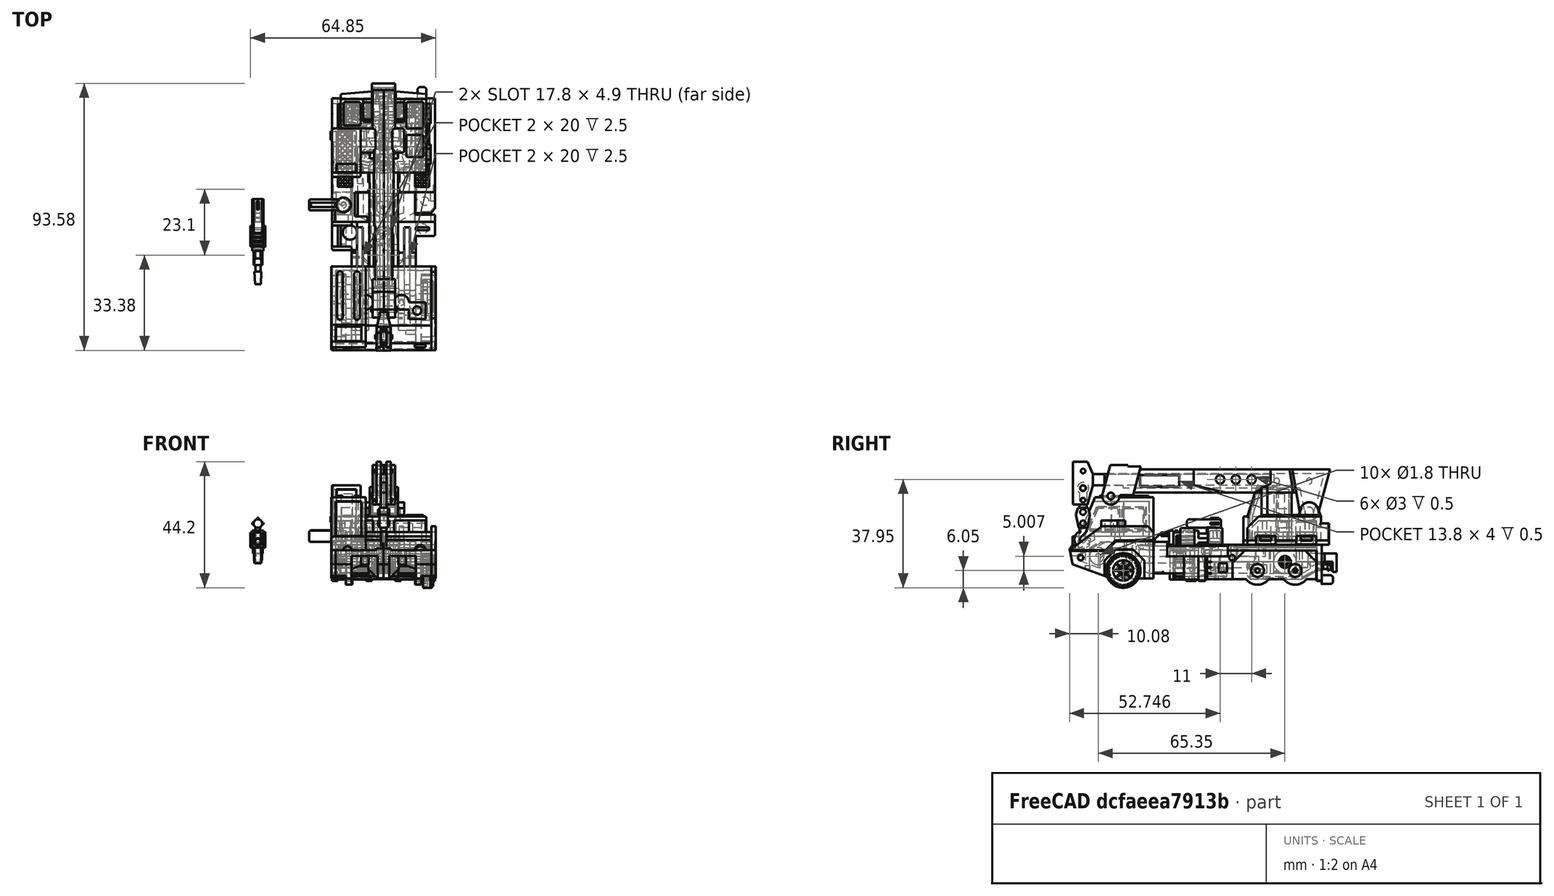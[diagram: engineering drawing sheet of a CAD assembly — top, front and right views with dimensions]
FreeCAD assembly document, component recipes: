
FREECAD ASSEMBLY — COMPONENT RECIPES ("Hook")

This assembly document has 27 components, labeled P0..P26 below (a component is one placed body or linked part). 27 of them carry a construction recipe — the FreeCAD feature program that regenerates the part from scratch, quoted from this document or its linked companion documents; the rest are supplied as boundary geometry only. No exploded tour is included for this assembly.
NOTE — document 2 of 5 of this assembly tour. The two overview renders and the header above are repeated from document 1; the component sections below continue where the previous document stopped.
COMPONENT P7 — recipe-attached ("Swivel_Base", modeled in this document).
Construction recipe (the document's own serialized feature program — sketch geometry with constraints, then the solid features built on it; lengths are millimeters unless a unit is written):

FEATURE [PartDesign::SubShapeBinder] Binder002
  BindCopyOnChange = 0
  BindMode = 2
  ClaimChildren = false
  Context = -> Body007 [Binder002.]
  Fuse = false
  MakeFace = true
  OffsetFill = false
  OffsetIntersection = false
  OffsetJoinType = 0
  OffsetOpenResult = false
  PartialLoad = false
  Refine = true
  Relative = true
  _Version = 2
FEATURE [Sketcher::SketchObject] Sketch080
  ArcFitTolerance = 1e-06
  AttachmentSupport = -> [Binder002]
  ExternalGeometry = -> [Binder002]
  FullyConstrained = true
  MakeInternals = false
  MapMode = 5
  Placement = pos=(0,0,5) rot=(0,0,1;0rad)
  sketch-geometry (2):
    g0: Circle CenterX=18.1 CenterY=30.5 CenterZ=0 NormalX=0 NormalY=0 NormalZ=1 AngleXU=0 Radius=5.55
    g1: Circle CenterX=18.1 CenterY=30.5 CenterZ=0 NormalX=0 NormalY=0 NormalZ=1 AngleXU=0 Radius=7
  constraints (6):
    c: Coincident(g0,g-4)
    c: Diameter(g-3) = 11
    c: Diameter(g-4) = 5
    c: Diameter(g0) = 11.1
    c: Coincident(g1,g0)
    c: Diameter(g1) = 14
FEATURE [PartDesign::Pad] Pad058
  Direction = (0,0,1)
  Length = 3
  Length2 = 10
  Profile = -> Sketch080
  ReferenceAxis = -> Sketch080 [N_Axis]
  Refine = true
  Reversed = true
  Suppressed = false
  Type = 0
FEATURE [Sketcher::SketchObject] Sketch081
  ArcFitTolerance = 1e-06
  AttachmentSupport = -> [Pad058]
  ExternalGeometry = -> [Pad058]
  FullyConstrained = true
  MakeInternals = false
  MapMode = 5
  Placement = pos=(0,0,5) rot=(0,0,1;0rad)
  sketch-geometry (1):
    g0: Circle CenterX=18.1 CenterY=30.5 CenterZ=0 NormalX=0 NormalY=0 NormalZ=1 AngleXU=0 Radius=7
  constraints (2):
    c: Coincident(g0,g-3)
    c: Equal(g0,g-3)
FEATURE [PartDesign::Pad] Pad059
  BaseFeature = -> Pad058
  Direction = (0,0,1)
  Length = 1.5
  Length2 = 10
  Profile = -> Sketch081
  ReferenceAxis = -> Sketch081 [N_Axis]
  Refine = true
  Suppressed = false
  Type = 0
FEATURE [Sketcher::SketchObject] Sketch082
  ArcFitTolerance = 1e-06
  AttachmentSupport = -> [Pad059]
  ExternalGeometry = -> [Pad059]
  FullyConstrained = true
  MakeInternals = false
  MapMode = 5
  Placement = pos=(0,0,6.5) rot=(0,0,1;0rad)
  sketch-geometry (1):
    g0: Circle CenterX=18.1 CenterY=30.5 CenterZ=0 NormalX=0 NormalY=0 NormalZ=1 AngleXU=0 Radius=2.25
  constraints (2):
    c: Coincident(g0,g-3)
    c: Diameter(g0) = 4.5
FEATURE [PartDesign::Pad] Pad060
  BaseFeature = -> Pad059
  Direction = (0,0,1)
  Length = 1.5
  Length2 = 10
  Profile = -> Sketch082
  ReferenceAxis = -> Sketch082 [N_Axis]
  Refine = true
  Suppressed = false
  Type = 0
FEATURE [Sketcher::SketchObject] Sketch083
  ArcFitTolerance = 1e-06
  AttachmentSupport = -> [Pad060]
  ExternalGeometry = -> [Pad060]
  FullyConstrained = true
  MakeInternals = false
  MapMode = 5
  Placement = pos=(0,0,8) rot=(0,0,1;0rad)
  sketch-geometry (1):
    g0: Circle CenterX=18.1 CenterY=30.5 CenterZ=0 NormalX=0 NormalY=0 NormalZ=1 AngleXU=0 Radius=0.75
  constraints (2):
    c: Coincident(g0,g-3)
    c: Diameter(g0) = 1.5
FEATURE [PartDesign::Pocket] Pocket032
  BaseFeature = -> Pad060
  Direction = (0,0,-1)
  Length = 5
  Length2 = 5
  Profile = -> Sketch083
  ReferenceAxis = -> Sketch083 [N_Axis]
  Refine = true
  Suppressed = false
  Type = 0
FEATURE [Sketcher::SketchObject] Sketch084
  ArcFitTolerance = 1e-06
  AttachmentSupport = -> [Pocket032]
  ExternalGeometry = -> [Pocket032]
  FullyConstrained = true
  MakeInternals = false
  MapMode = 5
  Placement = pos=(0,0,5) rot=(1,0,0;3.14159rad)
  sketch-geometry (1):
    g0: Circle CenterX=18.1 CenterY=-30.5 CenterZ=0 NormalX=0 NormalY=0 NormalZ=1 AngleXU=0 Radius=2.35
  constraints (2):
    c: Coincident(g0,g-4)
    c: Diameter(g0) = 4.7
FEATURE [PartDesign::Pad] Pad061
  BaseFeature = -> Pocket032
  Direction = (0,0,-1)
  Length = 3
  Length2 = 10
  Profile = -> Sketch084
  ReferenceAxis = -> Sketch084 [N_Axis]
  Refine = true
  Suppressed = false
  Type = 0
FEATURE [Sketcher::SketchObject] Sketch085
  ArcFitTolerance = 1e-06
  AttachmentSupport = -> [Pad061]
  ExternalGeometry = -> [Pad061]
  FullyConstrained = true
  MakeInternals = false
  MapMode = 5
  Placement = pos=(0,0,2) rot=(1,0,0;3.14159rad)
  sketch-geometry (1):
    g0: Circle CenterX=18.1 CenterY=-30.5 CenterZ=0 NormalX=0 NormalY=0 NormalZ=1 AngleXU=0 Radius=0.75
  constraints (2):
    c: Coincident(g0,g-3)
    c: Diameter(g0) = 1.5
FEATURE [PartDesign::Pocket] Pocket033
  BaseFeature = -> Pad061
  Direction = (0,0,1)
  Length = 5
  Length2 = 5
  Profile = -> Sketch085
  ReferenceAxis = -> Sketch085 [N_Axis]
  Refine = true
  Suppressed = false
  Type = 0
FEATURE [Sketcher::SketchObject] Sketch086
  ArcFitTolerance = 1e-06
  AttachmentSupport = -> [Pocket033]
  ExternalGeometry = -> [Pocket033]
  FullyConstrained = true
  MakeInternals = false
  MapMode = 5
  Placement = pos=(0,0,2) rot=(1,0,0;3.14159rad)
  sketch-geometry (9):
    g0: LineSegment StartX=33 StartY=-17.25 StartZ=0 EndX=10 EndY=-17.25 EndZ=0
    g1: LineSegment StartX=10 StartY=-17.25 StartZ=0 EndX=10 EndY=-15.75 EndZ=0
    g2: LineSegment StartX=10 StartY=-15.75 StartZ=0 EndX=0 EndY=-15.75 EndZ=0
    g3: LineSegment StartX=0 StartY=-15.75 StartZ=0 EndX=0 EndY=-32.75 EndZ=0
    g4: LineSegment StartX=0 StartY=-32.75 StartZ=0 EndX=3 EndY=-32.75 EndZ=0
    g5: LineSegment StartX=3 StartY=-32.75 StartZ=0 EndX=3 EndY=-45.75 EndZ=0
    g6: LineSegment StartX=3 StartY=-45.75 StartZ=0 EndX=33 EndY=-45.75 EndZ=0
    g7: LineSegment StartX=33 StartY=-45.75 StartZ=0 EndX=33 EndY=-17.25 EndZ=0
    g8: LineSegment [constr] StartX=18.1 StartY=-30.5 StartZ=0 EndX=18.1 EndY=-23.5 EndZ=0
  constraints (27):
    c: Horizontal(g0)
    c: Coincident(g1,g0)
    c: Vertical(g1)
    c: PointOnObject(g2,g-2)
    c: Horizontal(g2)
    c: Coincident(g3,g2)
    c: PointOnObject(g3,g-2)
    c: Coincident(g4,g3)
    c: Horizontal(g4)
    c: Coincident(g5,g4)
    c: Vertical(g5)
    c: Coincident(g6,g5)
    c: Horizontal(g6)
    c: Coincident(g7,g6)
    c: Coincident(g7,g0)
    c: Vertical(g7)
    c: DistanceX(g2,g2) = 10
    c: DistanceY(g3,g3) = 17
    c: Coincident(g2,g1)
    c: DistanceY(g1,g1) = 1.5
    c: DistanceY(g5,g5) = 13
    c: DistanceX(g4,g4) = 3
    c: DistanceX(g6,g6) = 30
    c: Coincident(g8,g-3)
    c: PointOnObject(g8,g-3)
    c: Vertical(g8)
    c: DistanceY(g8,g0) = 6.25
FEATURE [PartDesign::Pad] Pad062
  BaseFeature = -> Pocket033
  Direction = (0,0,-1)
  Length = 1.5
  Length2 = 10
  Profile = -> Sketch086
  ReferenceAxis = -> Sketch086 [N_Axis]
  Refine = true
  Reversed = true
  Suppressed = false
  Type = 0
FEATURE [Sketcher::SketchObject] Sketch087
  ArcFitTolerance = 1e-06
  AttachmentSupport = -> [Pad062]
  ExternalGeometry = -> [Pad062]
  FullyConstrained = true
  MakeInternals = false
  MapMode = 5
  Placement = pos=(0,0,3.5) rot=(0,0,1;0rad)
  sketch-geometry (4):
    g0: LineSegment StartX=14.6 StartY=45.75 StartZ=0 EndX=14.6 EndY=42.95 EndZ=0
    g1: LineSegment StartX=14.6 StartY=42.95 StartZ=0 EndX=21.6 EndY=42.95 EndZ=0
    g2: LineSegment StartX=21.6 StartY=42.95 StartZ=0 EndX=21.6 EndY=45.75 EndZ=0
    g3: LineSegment StartX=21.6 StartY=45.75 StartZ=0 EndX=14.6 EndY=45.75 EndZ=0
  constraints (12):
    c: Coincident(g0,g1)
    c: Coincident(g1,g2)
    c: Coincident(g2,g3)
    c: Coincident(g3,g0)
    c: Vertical(g0)
    c: Vertical(g2)
    c: Horizontal(g1)
    c: Horizontal(g3)
    c: PointOnObject(g0,g-3)
    c: DistanceX(g3,g3) = 7
    c: DistanceY(g2,g2) = 2.8
    c: DistanceX(g0,g-4) = 3.5
FEATURE [PartDesign::Pad] Pad063
  BaseFeature = -> Pad062
  Direction = (0,0,1)
  Length = 6
  Length2 = 10
  Profile = -> Sketch087
  ReferenceAxis = -> Sketch087 [N_Axis]
  Refine = true
  Suppressed = false
  Type = 0
FEATURE [Sketcher::SketchObject] Sketch088
  ArcFitTolerance = 1e-06
  AttachmentSupport = -> [Pad063]
  ExternalGeometry = -> [Pad063]
  FullyConstrained = true
  MakeInternals = false
  MapMode = 5
  Placement = pos=(0,0,3.5) rot=(0,0,1;0rad)
  sketch-geometry (2):
    g0: Circle CenterX=18.1 CenterY=38.9 CenterZ=0 NormalX=0 NormalY=0 NormalZ=1 AngleXU=0 Radius=1.55
    g1: Circle CenterX=4.95 CenterY=29.4 CenterZ=0 NormalX=0 NormalY=0 NormalZ=1 AngleXU=0 Radius=1.55
  constraints (6):
    c: Diameter(g0) = 3.1
    c: Diameter(g1) = 3.1
    c: DistanceX(g0,g-4) = 0
    c: DistanceY(g0,g-5) = 4.05
    c: DistanceX(g-6,g1) = 4.95
    c: DistanceY(g-7,g1) = 13.65
FEATURE [PartDesign::Pad] Pad064
  BaseFeature = -> Pad063
  Direction = (0,0,1)
  Length = 6.9
  Length2 = 10
  Profile = -> Sketch088
  ReferenceAxis = -> Sketch088 [N_Axis]
  Refine = true
  Suppressed = false
  Type = 0
FEATURE [Sketcher::SketchObject] Sketch089
  ArcFitTolerance = 1e-06
  AttachmentSupport = -> [Pad064]
  ExternalGeometry = -> [Pad064]
  FullyConstrained = true
  MakeInternals = false
  MapMode = 5
  Placement = pos=(0,0,3.5) rot=(0,0,1;0rad)
  sketch-geometry (8):
    g0: LineSegment StartX=31.5 StartY=39.75 StartZ=0 EndX=31.5 EndY=35.95 EndZ=0
    g1: LineSegment StartX=31.5 StartY=35.95 StartZ=0 EndX=34.5 EndY=35.95 EndZ=0
    g2: LineSegment StartX=34.5 StartY=35.95 StartZ=0 EndX=34.5 EndY=39.75 EndZ=0
    g3: LineSegment StartX=34.5 StartY=39.75 StartZ=0 EndX=31.5 EndY=39.75 EndZ=0
    g4: LineSegment StartX=31.5 StartY=25.55 StartZ=0 EndX=31.5 EndY=21.75 EndZ=0
    g5: LineSegment StartX=31.5 StartY=21.75 StartZ=0 EndX=34.5 EndY=21.75 EndZ=0
    g6: LineSegment StartX=34.5 StartY=21.75 StartZ=0 EndX=34.5 EndY=25.55 EndZ=0
    g7: LineSegment StartX=34.5 StartY=25.55 StartZ=0 EndX=31.5 EndY=25.55 EndZ=0
  constraints (25):
    c: Coincident(g0,g1)
    c: Coincident(g1,g2)
    c: Coincident(g2,g3)
    c: Coincident(g3,g0)
    c: Vertical(g0)
    c: Vertical(g2)
    c: Horizontal(g1)
    c: Horizontal(g3)
    c: Coincident(g4,g5)
    c: Coincident(g5,g6)
    c: Coincident(g6,g7)
    c: Coincident(g7,g4)
    c: Vertical(g4)
    c: Vertical(g6)
    c: Horizontal(g5)
    c: Horizontal(g7)
    c: DistanceY(g6,g6) = 3.8
    c: DistanceY(g2,g2) = 3.8
    c: DistanceX(g3,g3) = 3
    c: DistanceX(g7,g7) = 3
    c: DistanceX(g-5,g6) = 1.5
    c: DistanceX(g-4,g2) = 1.5
    c: DistanceY(g2,g-4) = 6
    c: DistanceY(g4,g0) = 10.4
    c: DistanceY(g-5,g5) = 4.5
FEATURE [PartDesign::Pad] Pad065
  BaseFeature = -> Pad064
  Direction = (0,0,1)
  Length = 1.5
  Length2 = 10
  Profile = -> Sketch089
  ReferenceAxis = -> Sketch089 [N_Axis]
  Refine = true
  Suppressed = false
  Type = 0
FEATURE [PartDesign::Pocket] Pocket034
  BaseFeature = -> Pad065
  Direction = (0,0,-1)
  Length = 8
  Length2 = 5
  Profile = -> Pad065 [Edge86]
  Refine = true
  Suppressed = false
  Type = 0
FEATURE [Sketcher::SketchObject] Sketch090
  ArcFitTolerance = 1e-06
  AttachmentSupport = -> [Pocket034]
  ExternalGeometry = -> [Pocket034]
  FullyConstrained = true
  MakeInternals = false
  MapMode = 5
  Placement = pos=(0,0,2) rot=(1,0,0;3.14159rad)
  sketch-geometry (1):
    g0: Circle CenterX=18.1 CenterY=-30.5 CenterZ=0 NormalX=0 NormalY=0 NormalZ=1 AngleXU=0 Radius=5.55
  constraints (2):
    c: Coincident(g0,g-3)
    c: Diameter(g0) = 11.1
FEATURE [PartDesign::Pocket] Pocket035
  BaseFeature = -> Pocket034
  Direction = (0,0,1)
  Length = 1.5
  Length2 = 5
  Profile = -> Sketch090
  ReferenceAxis = -> Sketch090 [N_Axis]
  Refine = true
  Suppressed = false
  Type = 0
FEATURE [PartDesign::Pad] Pad066
  BaseFeature = -> Pocket035
  Direction = (0,0,-1)
  Length = 1
  Length2 = 10
  Profile = -> Pocket035 [Face3]
  Refine = true
  Suppressed = false
  Type = 0
FEATURE [Sketcher::SketchObject] Sketch091
  ArcFitTolerance = 1e-06
  AttachmentSupport = -> [Pad066]
  ExternalGeometry = -> [Pad066]
  FullyConstrained = true
  MakeInternals = false
  MapMode = 5
  Placement = pos=(0,0,3.5) rot=(0,0,1;0rad)
  sketch-geometry (2):
    g0: Circle CenterX=12.5 CenterY=23.2 CenterZ=0 NormalX=0 NormalY=0 NormalZ=1 AngleXU=0 Radius=3.45
    g1: Circle CenterX=8.65 CenterY=38 CenterZ=0 NormalX=0 NormalY=0 NormalZ=1 AngleXU=0 Radius=3.45
  constraints (6):
    c: Diameter(g1) = 6.9
    c: Diameter(g0) = 6.9
    c: DistanceY(g1,g-4) = 7.75
    c: DistanceX(g-4,g1) = 5.65
    c: DistanceY(g-7,g0) = 7.45
    c: DistanceX(g-7,g0) = 12.5
FEATURE [PartDesign::Pad] Pad067
  BaseFeature = -> Pad066
  Direction = (0,0,1)
  Length = 3
  Length2 = 10
  Profile = -> Sketch091
  ReferenceAxis = -> Sketch091 [N_Axis]
  Refine = true
  Suppressed = false
  Type = 0
FEATURE [Sketcher::SketchObject] Sketch092
  ArcFitTolerance = 1e-06
  AttachmentSupport = -> [Pad067]
  ExternalGeometry = -> [Pad067]
  FullyConstrained = true
  MakeInternals = false
  MapMode = 5
  Placement = pos=(0,0,6.5) rot=(0,0,1;0rad)
  sketch-geometry (2):
    g0: Circle CenterX=8.65 CenterY=38 CenterZ=0 NormalX=0 NormalY=0 NormalZ=1 AngleXU=0 Radius=0.75
    g1: Circle CenterX=12.5 CenterY=23.2 CenterZ=0 NormalX=0 NormalY=0 NormalZ=1 AngleXU=0 Radius=0.75
  constraints (4):
    c: Coincident(g0,g-3)
    c: Coincident(g1,g-4)
    c: Radius(g0) = 0.75
    c: Radius(g1) = 0.75
FEATURE [PartDesign::Pocket] Pocket036
  BaseFeature = -> Pad067
  Direction = (0,0,-1)
  Length = 5
  Length2 = 5
  Profile = -> Sketch092
  ReferenceAxis = -> Sketch092 [N_Axis]
  Refine = true
  Suppressed = false
  Type = 0
FEATURE [Sketcher::SketchObject] Sketch093
  ArcFitTolerance = 1e-06
  AttachmentSupport = -> [Pocket036]
  ExternalGeometry = -> [Pocket036]
  FullyConstrained = true
  MakeInternals = false
  MapMode = 5
  Placement = pos=(0,0,6.5) rot=(0,0,1;0rad)
  sketch-geometry (2):
    g0: Circle CenterX=8.65 CenterY=38 CenterZ=0 NormalX=0 NormalY=0 NormalZ=1 AngleXU=0 Radius=2.4
    g1: Circle CenterX=12.5 CenterY=23.2 CenterZ=0 NormalX=0 NormalY=0 NormalZ=1 AngleXU=0 Radius=2.4
  constraints (4):
    c: Coincident(g0,g-3)
    c: Coincident(g1,g-4)
    c: Diameter(g0) = 4.8
    c: Diameter(g1) = 4.8
FEATURE [PartDesign::Pocket] Pocket037
  BaseFeature = -> Pocket036
  Direction = (0,0,-1)
  Length = 1
  Length2 = 5
  Profile = -> Sketch093
  ReferenceAxis = -> Sketch093 [N_Axis]
  Refine = true
  Suppressed = false
  Type = 0
FEATURE [Sketcher::SketchObject] Sketch094
  ArcFitTolerance = 1e-06
  AttachmentSupport = -> [Pocket037]
  ExternalGeometry = -> [Pocket037]
  FullyConstrained = false
  MakeInternals = false
  MapMode = 5
  Placement = pos=(0,0,2) rot=(1,0,0;3.14159rad)
  sketch-geometry (2):
    g0: Circle CenterX=12.5 CenterY=-23.2 CenterZ=0 NormalX=0 NormalY=0 NormalZ=1 AngleXU=0 Radius=2.15
    g1: Circle CenterX=8.65 CenterY=-38 CenterZ=0 NormalX=0 NormalY=0 NormalZ=1 AngleXU=0 Radius=2.15
  constraints (3):
    c: Diameter(g1) = 4.3
    c: Diameter(g0) = 4.3
    c: Coincident(g0,g-4)
FEATURE [PartDesign::Pocket] Pocket038
  BaseFeature = -> Pocket037
  Direction = (0,0,1)
  Length = 2
  Length2 = 5
  Profile = -> Sketch094
  ReferenceAxis = -> Sketch094 [N_Axis]
  Refine = true
  Suppressed = false
  Type = 0
FEATURE [Sketcher::SketchObject] Sketch096
  ArcFitTolerance = 1e-06
  AttachmentSupport = -> [Pocket038]
  ExternalGeometry = -> [Pocket038]
  FullyConstrained = true
  MakeInternals = false
  MapMode = 5
  Placement = pos=(0,0,3.5) rot=(0,0,1;0rad)
  sketch-geometry (6):
    g0: LineSegment StartX=14.6 StartY=45.75 StartZ=0 EndX=3 EndY=45.75 EndZ=0
    g1: LineSegment StartX=3 StartY=45.75 StartZ=0 EndX=3 EndY=44.75 EndZ=0
    g2: LineSegment StartX=3 StartY=44.75 StartZ=0 EndX=14.6 EndY=45.75 EndZ=0
    g3: LineSegment StartX=21.6 StartY=45.75 StartZ=0 EndX=33 EndY=45.75 EndZ=0
    g4: LineSegment StartX=33 StartY=45.75 StartZ=0 EndX=33 EndY=44.75 EndZ=0
    g5: LineSegment StartX=33 StartY=44.75 StartZ=0 EndX=21.6 EndY=45.75 EndZ=0
  constraints (14):
    c: Coincident(g0,g-3)
    c: Coincident(g0,g-4)
    c: Coincident(g1,g0)
    c: PointOnObject(g1,g-4)
    c: Coincident(g2,g1)
    c: Coincident(g2,g0)
    c: Coincident(g3,g-5)
    c: Coincident(g3,g-6)
    c: Coincident(g4,g3)
    c: PointOnObject(g4,g-6)
    c: Coincident(g5,g4)
    c: Coincident(g5,g3)
    c: DistanceY(g4,g4) = 1
    c: DistanceY(g1,g1) = 1
FEATURE [PartDesign::Pocket] Pocket041
  BaseFeature = -> Pocket038
  Direction = (0,0,-1)
  Length = 5
  Length2 = 5
  Profile = -> Sketch096
  ReferenceAxis = -> Sketch096 [N_Axis]
  Refine = true
  Suppressed = false
  Type = 0
FEATURE [Sketcher::SketchObject] Sketch104
  ArcFitTolerance = 1e-06
  AttachmentSupport = -> [Pocket041]
  ExternalGeometry = -> [Pocket041]
  FullyConstrained = true
  MakeInternals = false
  MapMode = 5
  Placement = pos=(0,0,5.5) rot=(0,0,1;0rad)
  sketch-geometry (2):
    g0: Circle CenterX=8.65 CenterY=38 CenterZ=0 NormalX=0 NormalY=0 NormalZ=1 AngleXU=0 Radius=1
    g1: Circle CenterX=12.5 CenterY=23.2 CenterZ=0 NormalX=0 NormalY=0 NormalZ=1 AngleXU=0 Radius=1
  constraints (4):
    c: Coincident(g0,g-3)
    c: Coincident(g1,g-4)
    c: Radius(g1) = 1
    c: Radius(g0) = 1
FEATURE [PartDesign::Pocket] Pocket043
  BaseFeature = -> Pocket041
  Direction = (0,0,-1)
  Length = 5
  Length2 = 5
  Profile = -> Sketch104
  ReferenceAxis = -> Sketch104 [N_Axis]
  Refine = true
  Suppressed = false
  Type = 0
FEATURE [Sketcher::SketchObject] Sketch105
  ArcFitTolerance = 1e-06
  AttachmentSupport = -> [Pocket043]
  ExternalGeometry = -> [Pocket043]
  FullyConstrained = true
  MakeInternals = false
  MapMode = 5
  Placement = pos=(0,0,3.5) rot=(0,0,1;0rad)
  sketch-geometry (8):
    g0: LineSegment StartX=14.6 StartY=45.75 StartZ=0 EndX=14.6 EndY=42.95 EndZ=0
    g1: LineSegment StartX=14.6 StartY=42.95 StartZ=0 EndX=14.1 EndY=42.95 EndZ=0
    g2: LineSegment StartX=14.1 StartY=42.95 StartZ=0 EndX=14.1 EndY=45.7069 EndZ=0
    g3: LineSegment StartX=14.1 StartY=45.7069 StartZ=0 EndX=14.6 EndY=45.75 EndZ=0
    g4: LineSegment StartX=21.6 StartY=45.75 StartZ=0 EndX=22.1 EndY=45.7061 EndZ=0
    g5: LineSegment StartX=22.1 StartY=45.7061 StartZ=0 EndX=22.1 EndY=42.95 EndZ=0
    g6: LineSegment StartX=22.1 StartY=42.95 StartZ=0 EndX=21.6 EndY=42.95 EndZ=0
    g7: LineSegment StartX=21.6 StartY=45.75 StartZ=0 EndX=21.6 EndY=42.95 EndZ=0
  constraints (20):
    c: Coincident(g0,g-6)
    c: Coincident(g0,g-6)
    c: Coincident(g1,g0)
    c: Horizontal(g1)
    c: Coincident(g2,g1)
    c: PointOnObject(g2,g-5)
    c: Vertical(g2)
    c: Coincident(g3,g2)
    c: Coincident(g3,g0)
    c: Coincident(g4,g-4)
    c: PointOnObject(g4,g-3)
    c: Coincident(g5,g4)
    c: Vertical(g5)
    c: Coincident(g6,g5)
    c: Coincident(g6,g-4)
    c: Horizontal(g6)
    c: DistanceX(g1,g1) = 0.5
    c: DistanceX(g6,g6) = 0.5
    c: Coincident(g7,g4)
    c: Coincident(g7,g6)
FEATURE [PartDesign::Pad] Pad076
  BaseFeature = -> Pocket043
  Direction = (0,0,1)
  Length = 6
  Length2 = 10
  Profile = -> Sketch105
  ReferenceAxis = -> Sketch105 [N_Axis]
  Refine = true
  Suppressed = false
  Type = 0
FEATURE [PartDesign::Fillet] Fillet003
  Base = -> Pad076 [Edge47,Edge45,Edge42,Edge38,Edge32,Edge49]
  BaseFeature = -> Pad076
  Radius = 0.5
  Refine = true
  SupportTransform = false
  Suppressed = false
  UseAllEdges = false
FEATURE [PartDesign::Pocket] Pocket045
  BaseFeature = -> Fillet003
  Direction = (0,0,1)
  Length = 0.6
  Length2 = 5
  Profile = -> Fillet003 [Face54]
  Refine = true
  Suppressed = false
  Type = 0
FEATURE [Sketcher::SketchObject] Sketch132
  ArcFitTolerance = 1e-06
  AttachmentSupport = -> [Pocket045]
  ExternalGeometry = -> [Pocket045]
  FullyConstrained = true
  MakeInternals = false
  MapMode = 5
  Placement = pos=(0,45.75,0) rot=(0,0.707107,0.707107;3.14159rad)
  sketch-geometry (3):
    g0: LineSegment StartX=-14.1 StartY=9.5 StartZ=0 EndX=-15.6 EndY=9.5 EndZ=0
    g1: LineSegment StartX=-15.6 StartY=9.5 StartZ=0 EndX=-14.1 EndY=8 EndZ=0
    g2: LineSegment StartX=-14.1 StartY=8 StartZ=0 EndX=-14.1 EndY=9.5 EndZ=0
  constraints (8):
    c: Coincident(g0,g-5)
    c: PointOnObject(g0,g-3)
    c: Coincident(g1,g0)
    c: PointOnObject(g1,g-5)
    c: Coincident(g2,g1)
    c: Coincident(g2,g0)
    c: DistanceX(g0,g0) = 1.5
    c: Angle(g1,g0) = 0.785398
FEATURE [PartDesign::Pocket] Pocket052
  BaseFeature = -> Pocket045
  Direction = (0,-1,2e-16)
  Length = 5
  Length2 = 5
  Profile = -> Sketch132
  ReferenceAxis = -> Sketch132 [N_Axis]
  Refine = true
  Suppressed = false
  Type = 0
FEATURE [PartDesign::Body] Body007  label="Swivel_Base"
  AllowCompound = false
  Group = -> [Binder002,Sketch080,Pad058,Sketch081,Pad059,Sketch082,Pad060,Sketch083,Pocket032,Sketch084,Pad061,Sketch085,Pocket033,Sketch086,Pad062,Sketch087,Pad063,Sketch088,Pad064,Sketch089,Pad065,Pocket034,Sketch090,Pocket035,Pad066,Sketch091,Pad067,Sketch092,Pocket036,Sketch093,Pocket037,Sketch094,Pocket038,Sketch096,Pocket041,Sketch104,Pocket043,Sketch105,Pad076,Fillet003,Pocket045,Sketch132,Pocket052]
  Origin = -> Origin007
  Tip = -> Pocket052
COMPONENT P8 — recipe-attached ("Rear_Cab", modeled in this document).
Construction recipe (the document's own serialized feature program — sketch geometry with constraints, then the solid features built on it; lengths are millimeters unless a unit is written):

FEATURE [PartDesign::SubShapeBinder] Binder003
  BindCopyOnChange = 0
  BindMode = 2
  ClaimChildren = false
  Context = -> Body008 [Binder003.]
  Fuse = false
  MakeFace = true
  OffsetFill = false
  OffsetIntersection = false
  OffsetJoinType = 0
  OffsetOpenResult = false
  PartialLoad = false
  Refine = true
  Relative = true
  _Version = 2
FEATURE [Sketcher::SketchObject] Sketch097
  ArcFitTolerance = 1e-06
  AttachmentSupport = -> [Binder003]
  ExternalGeometry = -> [Binder003]
  FullyConstrained = true
  MakeInternals = false
  MapMode = 5
  Placement = pos=(0,0,3.5) rot=(0,0,1;0rad)
  sketch-geometry (4):
    g0: LineSegment StartX=33 StartY=17.25 StartZ=0 EndX=10 EndY=17.25 EndZ=0
    g1: LineSegment StartX=33 StartY=18.75 StartZ=0 EndX=10 EndY=18.75 EndZ=0
    g2: LineSegment StartX=10 StartY=17.25 StartZ=0 EndX=10 EndY=18.75 EndZ=0
    g3: LineSegment StartX=33 StartY=17.25 StartZ=0 EndX=33 EndY=18.75 EndZ=0
  constraints (10):
    c: Horizontal(g1)
    c: DistanceY(g-16,g1) = 1.5
    c: Coincident(g2,g0)
    c: Coincident(g2,g1)
    c: Vertical(g2)
    c: Coincident(g3,g0)
    c: PointOnObject(g3,g-15)
    c: Coincident(g1,g3)
    c: Coincident(g0,g-16)
    c: Coincident(g0,g-17)
FEATURE [PartDesign::Pad] Pad068
  Direction = (0,0,1)
  Length = 4.5
  Length2 = 10
  Profile = -> Sketch097
  ReferenceAxis = -> Sketch097 [N_Axis]
  Refine = true
  Suppressed = false
  Type = 0
FEATURE [PartDesign::Pad] Pad069
  BaseFeature = -> Pad068
  Direction = (0,0,1)
  Length = 4.5
  Length2 = 10
  Profile = -> Sketch097
  ReferenceAxis = -> Sketch097 [N_Axis]
  Refine = true
  Suppressed = false
  Type = 0
FEATURE [Sketcher::SketchObject] Sketch098
  ArcFitTolerance = 1e-06
  AttachmentSupport = -> [Pad069]
  ExternalGeometry = -> [Pad069]
  FullyConstrained = true
  MakeInternals = false
  MapMode = 5
  Placement = pos=(33,0,0) rot=(0.57735,0.57735,0.57735;2.0944rad)
  sketch-geometry (4):
    g0: LineSegment StartX=17.25 StartY=8 StartZ=0 EndX=21.15 EndY=11.9 EndZ=0
    g1: LineSegment StartX=18.75 StartY=8 StartZ=0 EndX=22.65 EndY=11.9 EndZ=0
    g2: LineSegment StartX=22.65 StartY=11.9 StartZ=0 EndX=21.15 EndY=11.9 EndZ=0
    g3: LineSegment StartX=18.75 StartY=8 StartZ=0 EndX=17.25 EndY=8 EndZ=0
  constraints (10):
    c: Coincident(g0,g-3)
    c: Coincident(g1,g-3)
    c: Coincident(g2,g1)
    c: Coincident(g2,g0)
    c: Horizontal(g2)
    c: Angle(g-4,g1) = 2.35619
    c: Parallel(g0,g1)
    c: DistanceY(g-4,g1) = 8.4
    c: Coincident(g3,g1)
    c: Coincident(g3,g0)
FEATURE [PartDesign::Pad] Pad070
  BaseFeature = -> Pad069
  Direction = (1,0,0)
  Length = 23
  Length2 = 10
  Profile = -> Sketch098
  ReferenceAxis = -> Sketch098 [N_Axis]
  Refine = true
  Reversed = true
  Suppressed = false
  Type = 0
FEATURE [Sketcher::SketchObject] Sketch099
  ArcFitTolerance = 1e-06
  AttachmentSupport = -> [Pad070]
  ExternalGeometry = -> [Pad070,Binder003]
  FullyConstrained = true
  MakeInternals = false
  MapMode = 5
  Placement = pos=(0,0,11.9) rot=(0,0,1;0rad)
  sketch-geometry (10):
    g0: LineSegment StartX=33 StartY=21.15 StartZ=0 EndX=33 EndY=42.95 EndZ=0
    g1: LineSegment StartX=33 StartY=42.95 StartZ=0 EndX=22.28 EndY=42.95 EndZ=0
    g2: LineSegment StartX=22.28 StartY=42.95 StartZ=0 EndX=22.28 EndY=35.05 EndZ=0
    g3: LineSegment StartX=22.28 StartY=35.05 StartZ=0 EndX=13.93 EndY=35.05 EndZ=0
    g4: LineSegment StartX=13.93 StartY=35.05 StartZ=0 EndX=13.93 EndY=42.95 EndZ=0
    g5: LineSegment StartX=13.93 StartY=42.95 StartZ=0 EndX=3 EndY=42.95 EndZ=0
    g6: LineSegment StartX=3 StartY=42.95 StartZ=0 EndX=3 EndY=32.75 EndZ=0
    g7: LineSegment StartX=3 StartY=32.75 StartZ=0 EndX=10 EndY=32.75 EndZ=0
    g8: LineSegment StartX=10 StartY=32.75 StartZ=0 EndX=10 EndY=21.15 EndZ=0
    g9: LineSegment StartX=10 StartY=21.15 StartZ=0 EndX=33 EndY=21.15 EndZ=0
  constraints (27):
    c: Coincident(g0,g-3)
    c: Vertical(g0)
    c: Coincident(g1,g0)
    c: Horizontal(g1)
    c: Coincident(g2,g1)
    c: Vertical(g2)
    c: Coincident(g3,g2)
    c: Horizontal(g3)
    c: Coincident(g4,g3)
    c: Coincident(g5,g4)
    c: Horizontal(g5)
    c: PointOnObject(g5,g-4)
    c: Coincident(g6,g5)
    c: Coincident(g6,g-4)
    c: Coincident(g7,g6)
    c: Horizontal(g7)
    c: Coincident(g8,g7)
    c: Coincident(g8,g-3)
    c: Vertical(g8)
    c: Coincident(g9,g8)
    c: Coincident(g9,g0)
    c: Vertical(g4)
    c: DistanceY(g4,g-8) = 0
    c: DistanceY(g1,g-8) = 0
    c: DistanceY(g4,g4) = 7.9
    c: DistanceX(g5,g5) = 10.93
    c: DistanceX(g1,g1) = 10.72
FEATURE [PartDesign::Pad] Pad071
  BaseFeature = -> Pad070
  Direction = (0,0,1)
  Length = 1.5
  Length2 = 10
  Profile = -> Sketch099
  ReferenceAxis = -> Sketch099 [N_Axis]
  Refine = true
  Reversed = true
  Suppressed = false
  Type = 0
FEATURE [Sketcher::SketchObject] Sketch100
  ArcFitTolerance = 1e-06
  AttachmentSupport = -> [Pad071]
  ExternalGeometry = -> [Pad071]
  FullyConstrained = true
  MakeInternals = false
  MapMode = 5
  Placement = pos=(33,0,0) rot=(0.57735,0.57735,0.57735;2.0944rad)
  sketch-geometry (4):
    g0: LineSegment StartX=43.05 StartY=10.4 StartZ=0 EndX=41.45 EndY=10.4 EndZ=0
    g1: LineSegment StartX=41.45 StartY=10.4 StartZ=0 EndX=41.45 EndY=8 EndZ=0
    g2: LineSegment StartX=41.45 StartY=8 StartZ=0 EndX=43.05 EndY=8 EndZ=0
    g3: LineSegment StartX=43.05 StartY=8 StartZ=0 EndX=43.05 EndY=10.4 EndZ=0
  constraints (12):
    c: Coincident(g0,g1)
    c: Coincident(g1,g2)
    c: Coincident(g2,g3)
    c: Coincident(g3,g0)
    c: Horizontal(g0)
    c: Horizontal(g2)
    c: Vertical(g1)
    c: Vertical(g3)
    c: DistanceY(g1,g1) = 2.4
    c: DistanceX(g2,g2) = 1.6
    c: PointOnObject(g-3,g0)
    c: DistanceX(g-3,g0) = 0.1
FEATURE [PartDesign::Pad] Pad072
  BaseFeature = -> Pad071
  Direction = (1,0,0)
  Length = 10.72
  Length2 = 10
  Profile = -> Sketch100
  ReferenceAxis = -> Sketch100 [N_Axis]
  Refine = true
  Reversed = true
  Suppressed = false
  Type = 0
FEATURE [Sketcher::SketchObject] Sketch101
  ArcFitTolerance = 1e-06
  AttachmentSupport = -> [Pad072]
  ExternalGeometry = -> [Pad072]
  FullyConstrained = true
  MakeInternals = false
  MapMode = 5
  Placement = pos=(3,0,0) rot=(0.57735,-0.57735,-0.57735;2.0944rad)
  sketch-geometry (4):
    g0: LineSegment StartX=-43.05 StartY=10.4 StartZ=0 EndX=-43.05 EndY=8 EndZ=0
    g1: LineSegment StartX=-43.05 StartY=8 StartZ=0 EndX=-41.45 EndY=8 EndZ=0
    g2: LineSegment StartX=-41.45 StartY=8 StartZ=0 EndX=-41.45 EndY=10.4 EndZ=0
    g3: LineSegment StartX=-41.45 StartY=10.4 StartZ=0 EndX=-43.05 EndY=10.4 EndZ=0
  constraints (10):
    c: Coincident(g0,g1)
    c: Coincident(g1,g2)
    c: Coincident(g2,g3)
    c: Coincident(g3,g0)
    c: Vertical(g0)
    c: Vertical(g2)
    c: Horizontal(g1)
    c: Horizontal(g3)
    c: Coincident(g0,g-3)
    c: Coincident(g1,g-5)
FEATURE [PartDesign::Pad] Pad073
  BaseFeature = -> Pad072
  Direction = (-1,0,0)
  Length = 10.93
  Length2 = 10
  Profile = -> Sketch101
  ReferenceAxis = -> Sketch101 [N_Axis]
  Refine = true
  Reversed = true
  Suppressed = false
  Type = 0
FEATURE [Sketcher::SketchObject] Sketch102
  ArcFitTolerance = 1e-06
  AttachmentSupport = -> [Pad073]
  ExternalGeometry = -> [Pad073]
  FullyConstrained = true
  MakeInternals = false
  MapMode = 5
  Placement = pos=(0,0,10.4) rot=(0,0,1;0rad)
  sketch-geometry (8):
    g0: LineSegment StartX=13.93 StartY=43.05 StartZ=0 EndX=13.93 EndY=45.692 EndZ=0
    g1: LineSegment StartX=3 StartY=43.05 StartZ=0 EndX=3 EndY=44.75 EndZ=0
    g2: LineSegment StartX=3 StartY=44.75 StartZ=0 EndX=13.93 EndY=45.692 EndZ=0
    g3: LineSegment StartX=22.28 StartY=43.05 StartZ=0 EndX=22.28 EndY=45.691 EndZ=0
    g4: LineSegment StartX=22.28 StartY=45.691 StartZ=0 EndX=33 EndY=44.75 EndZ=0
    g5: LineSegment StartX=33 StartY=43.05 StartZ=0 EndX=33 EndY=44.75 EndZ=0
    g6: LineSegment StartX=3 StartY=43.05 StartZ=0 EndX=13.93 EndY=43.05 EndZ=0
    g7: LineSegment StartX=22.28 StartY=43.05 StartZ=0 EndX=33 EndY=43.05 EndZ=0
  constraints (20):
    c: Coincident(g0,g-3)
    c: Vertical(g0)
    c: Coincident(g1,g-3)
    c: Vertical(g1)
    c: Coincident(g2,g1)
    c: Coincident(g2,g0)
    c: Coincident(g3,g-4)
    c: Vertical(g3)
    c: Coincident(g4,g3)
    c: Coincident(g5,g-4)
    c: Coincident(g5,g4)
    c: Vertical(g5)
    c: DistanceY(g1,g1) = 1.7
    c: DistanceY(g0,g0) = 2.642
    c: Coincident(g6,g1)
    c: Coincident(g6,g0)
    c: Coincident(g7,g3)
    c: Coincident(g7,g5)
    c: DistanceY(g5,g5) = 1.7
    c: DistanceY(g3,g3) = 2.641
FEATURE [PartDesign::Pad] Pad074
  BaseFeature = -> Pad073
  Direction = (0,0,1)
  Length = 6.9
  Length2 = 10
  Profile = -> Sketch102
  ReferenceAxis = -> Sketch102 [N_Axis]
  Refine = true
  Reversed = true
  Suppressed = false
  Type = 0
FEATURE [PartDesign::Pocket] Pocket042
  BaseFeature = -> Pad074
  Direction = (0,0,-1)
  Length = 0.9
  Length2 = 5
  Profile = -> Pad074 [Face25,Face24]
  Refine = true
  Suppressed = false
  Type = 0
FEATURE [Sketcher::SketchObject] Sketch103
  ArcFitTolerance = 1e-06
  AttachmentSupport = -> [Pocket042]
  ExternalGeometry = -> [Pocket042]
  FullyConstrained = true
  MakeInternals = false
  MapMode = 5
  Placement = pos=(33,0,0) rot=(0.57735,0.57735,0.57735;2.0944rad)
  sketch-geometry (15):
    g0: LineSegment StartX=18.75 StartY=3.5 StartZ=0 EndX=18.75 EndY=8 EndZ=0
    g1: LineSegment StartX=18.75 StartY=8 StartZ=0 EndX=21.15 EndY=10.4 EndZ=0
    g2: LineSegment StartX=21.15 StartY=10.4 StartZ=0 EndX=41.45 EndY=10.4 EndZ=0
    g3: LineSegment StartX=41.45 StartY=10.4 StartZ=0 EndX=41.45 EndY=8 EndZ=0
    g4: LineSegment StartX=41.45 StartY=8 StartZ=0 EndX=43.05 EndY=8 EndZ=0
    g5: LineSegment StartX=43.05 StartY=8 StartZ=0 EndX=43.05 EndY=3.5 EndZ=0
    g6: LineSegment StartX=43.05 StartY=3.5 StartZ=0 EndX=39.8 EndY=3.5 EndZ=0
    g7: LineSegment StartX=39.8 StartY=3.5 StartZ=0 EndX=39.8 EndY=5.1 EndZ=0
    g8: LineSegment StartX=39.8 StartY=5.1 StartZ=0 EndX=35.9 EndY=5.1 EndZ=0
    g9: LineSegment StartX=35.9 StartY=5.1 StartZ=0 EndX=35.9 EndY=3.5 EndZ=0
    g10: LineSegment StartX=35.9 StartY=3.5 StartZ=0 EndX=25.6 EndY=3.5 EndZ=0
    g11: LineSegment StartX=25.6 StartY=3.5 StartZ=0 EndX=25.6 EndY=5.1 EndZ=0
    g12: LineSegment StartX=25.6 StartY=5.1 StartZ=0 EndX=21.7 EndY=5.1 EndZ=0
    g13: LineSegment StartX=21.7 StartY=5.1 StartZ=0 EndX=21.7 EndY=3.5 EndZ=0
    g14: LineSegment StartX=21.7 StartY=3.5 StartZ=0 EndX=18.75 EndY=3.5 EndZ=0
  constraints (38):
    c: Coincident(g0,g-3)
    c: Coincident(g0,g-4)
    c: Coincident(g1,g0)
    c: Coincident(g1,g-5)
    c: Coincident(g2,g1)
    c: Coincident(g2,g-6)
    c: Coincident(g3,g2)
    c: Coincident(g3,g-7)
    c: Coincident(g4,g3)
    c: Coincident(g4,g-8)
    c: Coincident(g5,g4)
    c: Coincident(g5,g-8)
    c: Coincident(g6,g5)
    c: Horizontal(g6)
    c: Coincident(g7,g6)
    c: Vertical(g7)
    c: Coincident(g8,g7)
    c: Horizontal(g8)
    c: Coincident(g9,g8)
    c: Vertical(g9)
    c: Coincident(g10,g9)
    c: Horizontal(g10)
    c: Coincident(g11,g10)
    c: Vertical(g11)
    c: Coincident(g12,g11)
    c: Horizontal(g12)
    c: Coincident(g13,g12)
    c: Vertical(g13)
    c: Coincident(g14,g13)
    c: Coincident(g14,g0)
    c: Horizontal(g14)
    c: DistanceX(g6,g6) = 3.25
    c: DistanceX(g8,g8) = 3.9
    c: DistanceX(g12,g12) = 3.9
    c: DistanceY(g9,g9) = 1.6
    c: DistanceY(g11,g11) = 1.6
    c: DistanceX(g14,g14) = 2.95
    c: DistanceY(g13,g13) = 1.6
FEATURE [PartDesign::Pad] Pad075
  BaseFeature = -> Pocket042
  Direction = (1,0,0)
  Length = 1.5
  Length2 = 10
  Profile = -> Sketch103
  ReferenceAxis = -> Sketch103 [N_Axis]
  Refine = true
  Reversed = true
  Suppressed = false
  Type = 0
FEATURE [Sketcher::SketchObject] Sketch106
  ArcFitTolerance = 1e-06
  AttachmentSupport = -> [Pad075]
  ExternalGeometry = -> [Pad075]
  FullyConstrained = true
  MakeInternals = false
  MapMode = 5
  Placement = pos=(0,0,10.4) rot=(1,0,0;3.14159rad)
  sketch-geometry (2):
    g0: Circle CenterX=12.5 CenterY=-23.2 CenterZ=0 NormalX=0 NormalY=0 NormalZ=1 AngleXU=0 Radius=2.3
    g1: Circle CenterX=8.65 CenterY=-38 CenterZ=0 NormalX=0 NormalY=0 NormalZ=1 AngleXU=0 Radius=2.3
  constraints (6):
    c: Radius(g0) = 2.3
    c: Radius(g1) = 2.3
    c: DistanceX(g-4,g0) = 2.5
    c: DistanceY(g0,g-4) = 2.05
    c: DistanceX(g-3,g1) = 5.65
    c: DistanceY(g1,g-3) = 5.25
FEATURE [PartDesign::Pad] Pad077
  BaseFeature = -> Pad075
  Direction = (0,0,-1)
  Length = 4.9
  Length2 = 10
  Profile = -> Sketch106
  ReferenceAxis = -> Sketch106 [N_Axis]
  Refine = true
  Suppressed = false
  Type = 0
FEATURE [Sketcher::SketchObject] Sketch107
  ArcFitTolerance = 1e-06
  AttachmentSupport = -> [Pad077]
  ExternalGeometry = -> [Pad077]
  FullyConstrained = true
  MakeInternals = false
  MapMode = 5
  Placement = pos=(0,0,5.5) rot=(1,0,0;3.14159rad)
  sketch-geometry (2):
    g0: Circle CenterX=8.65 CenterY=-38 CenterZ=0 NormalX=0 NormalY=0 NormalZ=1 AngleXU=0 Radius=0.75
    g1: Circle CenterX=12.5 CenterY=-23.2 CenterZ=0 NormalX=0 NormalY=0 NormalZ=1 AngleXU=0 Radius=0.75
  constraints (4):
    c: Coincident(g0,g-4)
    c: Coincident(g1,g-3)
    c: Radius(g1) = 0.75
    c: Radius(g0) = 0.75
FEATURE [PartDesign::Pocket] Pocket044
  BaseFeature = -> Pad077
  Direction = (0,0,1)
  Length = 4.9
  Length2 = 5
  Profile = -> Sketch107
  ReferenceAxis = -> Sketch107 [N_Axis]
  Refine = true
  Suppressed = false
  Type = 0
FEATURE [Sketcher::SketchObject] Sketch108
  ArcFitTolerance = 1e-06
  AttachmentSupport = -> [Pocket044]
  ExternalGeometry = -> [Pocket044]
  FullyConstrained = true
  MakeInternals = false
  MapMode = 5
  Placement = pos=(33,0,-2.28e-14) rot=(0.57735,0.57735,0.57735;2.0944rad)
  sketch-geometry (16):
    g0: LineSegment StartX=21.7 StartY=5.1 StartZ=0 EndX=21.7 EndY=3.4 EndZ=0
    g1: LineSegment StartX=21.7 StartY=3.4 StartZ=0 EndX=25.6 EndY=3.4 EndZ=0
    g2: LineSegment StartX=25.6 StartY=3.4 StartZ=0 EndX=25.6 EndY=5.1 EndZ=0
    g3: LineSegment StartX=25.6 StartY=5.1 StartZ=0 EndX=27.1 EndY=5.1 EndZ=0
    g4: LineSegment StartX=27.1 StartY=5.1 StartZ=0 EndX=27.1 EndY=2.1 EndZ=0
    g5: LineSegment StartX=27.1 StartY=2.1 StartZ=0 EndX=20.2 EndY=2.1 EndZ=0
    g6: LineSegment StartX=20.2 StartY=2.1 StartZ=0 EndX=20.2 EndY=5.1 EndZ=0
    g7: LineSegment StartX=21.7 StartY=5.1 StartZ=0 EndX=20.2 EndY=5.1 EndZ=0
    g8: LineSegment StartX=35.9 StartY=5.1 StartZ=0 EndX=35.9 EndY=3.4 EndZ=0
    g9: LineSegment StartX=35.9 StartY=3.4 StartZ=0 EndX=39.8 EndY=3.4 EndZ=0
    g10: LineSegment StartX=39.8 StartY=3.4 StartZ=0 EndX=39.8 EndY=5.1 EndZ=0
    g11: LineSegment StartX=39.8 StartY=5.1 StartZ=0 EndX=41.3 EndY=5.1 EndZ=0
    g12: LineSegment StartX=41.3 StartY=5.1 StartZ=0 EndX=41.3 EndY=2.1 EndZ=0
    g13: LineSegment StartX=41.3 StartY=2.1 StartZ=0 EndX=34.4 EndY=2.1 EndZ=0
    g14: LineSegment StartX=34.4 StartY=2.1 StartZ=0 EndX=34.4 EndY=5.1 EndZ=0
    g15: LineSegment StartX=35.9 StartY=5.1 StartZ=0 EndX=34.4 EndY=5.1 EndZ=0
  constraints (44):
    c: Coincident(g0,g-8)
    c: Vertical(g0)
    c: Coincident(g1,g0)
    c: Horizontal(g1)
    c: Coincident(g2,g1)
    c: Coincident(g2,g-7)
    c: Vertical(g2)
    c: Coincident(g3,g2)
    c: Horizontal(g3)
    c: Coincident(g4,g3)
    c: Vertical(g4)
    c: Coincident(g5,g4)
    c: Horizontal(g5)
    c: Coincident(g6,g5)
    c: Vertical(g6)
    c: Coincident(g7,g0)
    c: Coincident(g7,g6)
    c: Horizontal(g7)
    c: DistanceX(g7,g7) = 1.5
    c: DistanceX(g3,g3) = 1.5
    c: DistanceY(g0,g0) = 1.7
    c: DistanceY(g6,g6) = 3
    c: Coincident(g8,g-5)
    c: Vertical(g8)
    c: Coincident(g9,g8)
    c: Horizontal(g9)
    c: Coincident(g10,g9)
    c: Coincident(g10,g-4)
    c: Vertical(g10)
    c: Coincident(g11,g10)
    c: Horizontal(g11)
    c: Coincident(g12,g11)
    c: Vertical(g12)
    c: Coincident(g13,g12)
    c: Horizontal(g13)
    c: Coincident(g14,g13)
    c: Vertical(g14)
    c: Coincident(g15,g8)
    c: Coincident(g15,g14)
    c: Horizontal(g15)
    c: DistanceX(g15,g15) = 1.5
    c: DistanceX(g11,g11) = 1.5
    c: DistanceY(g14,g14) = 3
    c: DistanceY(g8,g8) = 1.7
FEATURE [PartDesign::Pad] Pad078
  BaseFeature = -> Pocket044
  Direction = (1,0,0)
  Length = 1.5
  Length2 = 10
  Profile = -> Sketch108
  ReferenceAxis = -> Sketch108 [N_Axis]
  Refine = true
  Suppressed = false
  Type = 0
FEATURE [Sketcher::SketchObject] Sketch109
  ArcFitTolerance = 1e-06
  AttachmentSupport = -> [Pad078]
  ExternalGeometry = -> [Pad078]
  FullyConstrained = true
  MakeInternals = false
  MapMode = 5
  Placement = pos=(3,0,0) rot=(0.57735,-0.57735,-0.57735;2.0944rad)
  sketch-geometry (6):
    g0: LineSegment StartX=-43.05 StartY=3.5 StartZ=0 EndX=-43.05 EndY=8 EndZ=0
    g1: LineSegment StartX=-43.05 StartY=8 StartZ=0 EndX=-41.45 EndY=8 EndZ=0
    g2: LineSegment StartX=-41.45 StartY=8 StartZ=0 EndX=-41.45 EndY=10.4 EndZ=0
    g3: LineSegment StartX=-41.45 StartY=10.4 StartZ=0 EndX=-32.75 EndY=10.4 EndZ=0
    g4: LineSegment StartX=-32.75 StartY=10.4 StartZ=0 EndX=-32.75 EndY=3.5 EndZ=0
    g5: LineSegment StartX=-43.05 StartY=3.5 StartZ=0 EndX=-32.75 EndY=3.5 EndZ=0
  constraints (13):
    c: Coincident(g0,g-6)
    c: Coincident(g0,g-6)
    c: Coincident(g1,g0)
    c: Coincident(g1,g-5)
    c: Coincident(g2,g1)
    c: Coincident(g2,g-4)
    c: Coincident(g3,g2)
    c: Coincident(g3,g-3)
    c: Coincident(g4,g3)
    c: Vertical(g4)
    c: Coincident(g5,g0)
    c: Coincident(g5,g4)
    c: Horizontal(g5)
FEATURE [PartDesign::Pad] Pad079
  BaseFeature = -> Pad078
  Direction = (-1,0,0)
  Length = 1.5
  Length2 = 10
  Profile = -> Sketch109
  ReferenceAxis = -> Sketch109 [N_Axis]
  Refine = true
  Reversed = true
  Suppressed = false
  Type = 0
FEATURE [Sketcher::SketchObject] Sketch110
  ArcFitTolerance = 1e-06
  AttachmentOffset = pos=(0,0,-8.4) rot=(0,0,1;0rad)
  AttachmentSupport = -> [Pad079]
  ExternalGeometry = -> [Pad079]
  FullyConstrained = true
  MakeInternals = false
  MapMode = 5
  Placement = pos=(0,0,3.5) rot=(0,0,1;0rad)
  sketch-geometry (10):
    g0: LineSegment StartX=4.5 StartY=32.75 StartZ=0 EndX=4.5 EndY=31.25 EndZ=0
    g1: LineSegment StartX=4.5 StartY=31.25 StartZ=0 EndX=1.5 EndY=31.25 EndZ=0
    g2: LineSegment StartX=1.5 StartY=31.25 StartZ=0 EndX=1.5 EndY=17.25 EndZ=0
    g3: LineSegment StartX=1.5 StartY=17.25 StartZ=0 EndX=8.5 EndY=17.25 EndZ=0
    g4: LineSegment StartX=8.5 StartY=17.25 StartZ=0 EndX=8.5 EndY=18.75 EndZ=0
    g5: LineSegment StartX=8.5 StartY=18.75 StartZ=0 EndX=10 EndY=18.75 EndZ=0
    g6: LineSegment StartX=10 StartY=18.75 StartZ=0 EndX=10 EndY=15.75 EndZ=0
    g7: LineSegment StartX=10 StartY=15.75 StartZ=0 EndX=0 EndY=15.75 EndZ=0
    g8: LineSegment StartX=0 StartY=15.75 StartZ=0 EndX=0 EndY=32.75 EndZ=0
    g9: LineSegment StartX=0 StartY=32.75 StartZ=0 EndX=4.5 EndY=32.75 EndZ=0
  constraints (29):
    c: PointOnObject(g0,g-3)
    c: Vertical(g0)
    c: Coincident(g1,g0)
    c: Horizontal(g1)
    c: Coincident(g2,g1)
    c: Vertical(g2)
    c: Coincident(g3,g2)
    c: Horizontal(g3)
    c: Coincident(g4,g3)
    c: Vertical(g4)
    c: Coincident(g5,g4)
    c: Horizontal(g5)
    c: Coincident(g6,g5)
    c: Vertical(g6)
    c: Coincident(g7,g6)
    c: PointOnObject(g7,g-2)
    c: Horizontal(g7)
    c: Coincident(g8,g7)
    c: PointOnObject(g8,g-2)
    c: Coincident(g9,g8)
    c: Coincident(g9,g0)
    c: Horizontal(g9)
    c: DistanceX(g-3,g0) = 1.5
    c: DistanceY(g1,g8) = 1.5
    c: DistanceX(g8,g1) = 1.5
    c: DistanceX(g3,g6) = 1.5
    c: Coincident(g5,g-5)
    c: DistanceY(g7,g2) = 1.5
    c: DistanceY(g6,g-4) = 1.5
FEATURE [PartDesign::Pad] Pad080
  BaseFeature = -> Pad079
  Direction = (0,0,1)
  Length = 8.4
  Length2 = 10
  Profile = -> Sketch110
  ReferenceAxis = -> Sketch110 [N_Axis]
  Refine = true
  Suppressed = false
  Type = 0
FEATURE [PartDesign::Pad] Pad081
  BaseFeature = -> Pad080
  Direction = (-1,0,0)
  Length = 1.5
  Length2 = 10
  Profile = -> Pad080 [Face24]
  Refine = true
  Suppressed = false
  Type = 0
FEATURE [Sketcher::SketchObject] Sketch111
  ArcFitTolerance = 1e-06
  AttachmentSupport = -> [Pad081]
  ExternalGeometry = -> [Pad081]
  FullyConstrained = true
  MakeInternals = false
  MapMode = 5
  Placement = pos=(10,0,0) rot=(0.57735,0.57735,0.57735;2.0944rad)
  sketch-geometry (3):
    g0: LineSegment StartX=18.75 StartY=11.9 StartZ=0 EndX=18.75 EndY=9.5 EndZ=0
    g1: LineSegment StartX=18.75 StartY=9.5 StartZ=0 EndX=21.15 EndY=11.9 EndZ=0
    g2: LineSegment StartX=21.15 StartY=11.9 StartZ=0 EndX=18.75 EndY=11.9 EndZ=0
  constraints (6):
    c: Coincident(g0,g-3)
    c: Coincident(g0,g-4)
    c: Coincident(g1,g0)
    c: Coincident(g1,g-4)
    c: Coincident(g2,g1)
    c: Coincident(g2,g0)
FEATURE [PartDesign::Pad] Pad082
  BaseFeature = -> Pad081
  Direction = (1,0,0)
  Length = 1.5
  Length2 = 10
  Profile = -> Sketch111
  ReferenceAxis = -> Sketch111 [N_Axis]
  Refine = true
  Reversed = true
  Suppressed = false
  Type = 0
FEATURE [PartDesign::Pad] Pad083
  BaseFeature = -> Pad082
  Direction = (0,-1,0)
  Length = 1.5
  Length2 = 10
  Profile = -> Pad082 [Face38]
  Refine = true
  Suppressed = false
  Type = 0
FEATURE [Sketcher::SketchObject] Sketch112
  ArcFitTolerance = 1e-06
  AttachmentSupport = -> [Pad083]
  ExternalGeometry = -> [Pad083]
  FullyConstrained = true
  MakeInternals = false
  MapMode = 5
  Placement = pos=(10,0,0) rot=(0.57735,0.57735,0.57735;2.0944rad)
  sketch-geometry (4):
    g0: LineSegment StartX=17.25 StartY=11.9 StartZ=0 EndX=20.75 EndY=22.9 EndZ=0
    g1: LineSegment StartX=20.75 StartY=22.9 StartZ=0 EndX=32.75 EndY=22.9 EndZ=0
    g2: LineSegment StartX=17.25 StartY=11.9 StartZ=0 EndX=32.75 EndY=11.9 EndZ=0
    g3: LineSegment StartX=32.75 StartY=11.9 StartZ=0 EndX=32.75 EndY=22.9 EndZ=0
  constraints (11):
    c: PointOnObject(g0,g-3)
    c: Coincident(g1,g0)
    c: Horizontal(g1)
    c: DistanceY(g-5,g1) = 11
    c: DistanceX(g-4,g0) = 1.5
    c: DistanceX(g1,g1) = 12
    c: Coincident(g2,g0)
    c: Coincident(g2,g-6)
    c: Coincident(g3,g2)
    c: Coincident(g3,g1)
    c: Vertical(g3)
FEATURE [PartDesign::Pad] Pad084
  BaseFeature = -> Pad083
  Direction = (1,0,0)
  Length = 1.5
  Length2 = 10
  Profile = -> Sketch112
  ReferenceAxis = -> Sketch112 [N_Axis]
  Refine = true
  Reversed = true
  Suppressed = false
  Type = 0
FEATURE [Sketcher::SketchObject] Sketch113
  ArcFitTolerance = 1e-06
  AttachmentSupport = -> [Pad084]
  ExternalGeometry = -> [Pad084]
  FullyConstrained = true
  MakeInternals = false
  MapMode = 5
  Placement = pos=(8.5,0,0) rot=(0.57735,-0.57735,-0.57735;2.0944rad)
  sketch-geometry (4):
    g0: LineSegment StartX=-32.75 StartY=22.9 StartZ=0 EndX=-32.75 EndY=11.9 EndZ=0
    g1: LineSegment StartX=-32.75 StartY=11.9 StartZ=0 EndX=-31.25 EndY=11.9 EndZ=0
    g2: LineSegment StartX=-31.25 StartY=11.9 StartZ=0 EndX=-31.25 EndY=22.9 EndZ=0
    g3: LineSegment StartX=-31.25 StartY=22.9 StartZ=0 EndX=-32.75 EndY=22.9 EndZ=0
  constraints (10):
    c: Coincident(g0,g1)
    c: Coincident(g1,g2)
    c: Coincident(g2,g3)
    c: Coincident(g3,g0)
    c: Vertical(g2)
    c: Horizontal(g1)
    c: Horizontal(g3)
    c: Coincident(g0,g-4)
    c: DistanceX(g1,g1) = 1.5
    c: Coincident(g0,g-4)
FEATURE [PartDesign::Pad] Pad085
  BaseFeature = -> Pad084
  Direction = (-1,0,0)
  Length = 8.5
  Length2 = 10
  Profile = -> Sketch113
  ReferenceAxis = -> Sketch113 [N_Axis]
  Refine = true
  Suppressed = false
  Type = 0
FEATURE [Sketcher::SketchObject] Sketch114
  ArcFitTolerance = 1e-06
  AttachmentSupport = -> [Pad085]
  ExternalGeometry = -> [Pad085]
  FullyConstrained = true
  MakeInternals = false
  MapMode = 5
  Placement = pos=(8.5,0,0) rot=(0.57735,-0.57735,-0.57735;2.0944rad)
  sketch-geometry (4):
    g0: LineSegment StartX=-31.25 StartY=22.9 StartZ=0 EndX=-20.75 EndY=22.9 EndZ=0
    g1: LineSegment StartX=-20.75 StartY=22.9 StartZ=0 EndX=-20.2727 EndY=21.4 EndZ=0
    g2: LineSegment StartX=-20.2727 StartY=21.4 StartZ=0 EndX=-31.25 EndY=21.4 EndZ=0
    g3: LineSegment StartX=-31.25 StartY=21.4 StartZ=0 EndX=-31.25 EndY=22.9 EndZ=0
  constraints (10):
    c: Coincident(g0,g-4)
    c: Coincident(g1,g0)
    c: PointOnObject(g1,g-4)
    c: Coincident(g2,g1)
    c: PointOnObject(g2,g-5)
    c: Horizontal(g2)
    c: Coincident(g3,g2)
    c: Coincident(g3,g0)
    c: Coincident(g0,g-5)
    c: DistanceY(g3,g3) = 1.5
FEATURE [PartDesign::Pad] Pad086
  BaseFeature = -> Pad085
  Direction = (-1,0,0)
  Length = 8.5
  Length2 = 10
  Profile = -> Sketch114
  ReferenceAxis = -> Sketch114 [N_Axis]
  Refine = true
  Suppressed = false
  Type = 0
FEATURE [Sketcher::SketchObject] Sketch115
  ArcFitTolerance = 1e-06
  AttachmentSupport = -> [Pad086]
  ExternalGeometry = -> [Pad086]
  FullyConstrained = true
  MakeInternals = false
  MapMode = 5
  Placement = pos=(1.3e-15,0,0) rot=(0.57735,-0.57735,-0.57735;2.0944rad)
  sketch-geometry (4):
    g0: LineSegment StartX=-20.2727 StartY=21.4 StartZ=0 EndX=-17.25 EndY=11.9 EndZ=0
    g1: LineSegment StartX=-17.25 StartY=11.9 StartZ=0 EndX=-31.25 EndY=11.9 EndZ=0
    g2: LineSegment StartX=-20.2727 StartY=21.4 StartZ=0 EndX=-31.25 EndY=21.4 EndZ=0
    g3: LineSegment StartX=-31.25 StartY=21.4 StartZ=0 EndX=-31.25 EndY=11.9 EndZ=0
  constraints (8):
    c: Coincident(g0,g-6)
    c: Coincident(g0,g-6)
    c: Coincident(g1,g0)
    c: Coincident(g1,g-5)
    c: Coincident(g2,g0)
    c: Coincident(g2,g-4)
    c: Coincident(g3,g2)
    c: Coincident(g3,g1)
FEATURE [PartDesign::Pad] Pad087
  BaseFeature = -> Pad086
  Direction = (-1,0,0)
  Length = 1.5
  Length2 = 10
  Profile = -> Sketch115
  ReferenceAxis = -> Sketch115 [N_Axis]
  Refine = true
  Reversed = true
  Suppressed = false
  Type = 0
FEATURE [Sketcher::SketchObject] Sketch116
  ArcFitTolerance = 1e-06
  AttachmentSupport = -> [Pad087]
  ExternalGeometry = -> [Pad087]
  FullyConstrained = true
  MakeInternals = false
  MapMode = 5
  Placement = pos=(9e-16,0,0) rot=(0.57735,-0.57735,-0.57735;2.0944rad)
  sketch-geometry (9):
    g0: LineSegment StartX=-31.25 StartY=21.4 StartZ=0 EndX=-31.25 EndY=14.7 EndZ=0
    g1: LineSegment StartX=-31.25 StartY=14.7 StartZ=0 EndX=-28.05 EndY=14.7 EndZ=0
    g2: LineSegment StartX=-28.05 StartY=14.7 StartZ=0 EndX=-28.05 EndY=21.4 EndZ=0
    g3: LineSegment StartX=-28.05 StartY=21.4 StartZ=0 EndX=-31.25 EndY=21.4 EndZ=0
    g4: LineSegment StartX=-26.55 StartY=21.4 StartZ=0 EndX=-26.55 EndY=11.9 EndZ=0
    g5: LineSegment StartX=-26.55 StartY=11.9 StartZ=0 EndX=-18.8241 EndY=11.9 EndZ=0
    g6: LineSegment StartX=-18.8241 StartY=11.9 StartZ=0 EndX=-21.8468 EndY=21.4 EndZ=0
    g7: LineSegment StartX=-21.8468 StartY=21.4 StartZ=0 EndX=-26.55 EndY=21.4 EndZ=0
    g8: LineSegment [constr] StartX=-19.5372 StartY=19.0883 StartZ=0 EndX=-20.9666 EndY=18.6335 EndZ=0
  constraints (28):
    c: Coincident(g0,g1)
    c: Coincident(g1,g2)
    c: Coincident(g2,g3)
    c: Coincident(g3,g0)
    c: Vertical(g0)
    c: Vertical(g2)
    c: Horizontal(g1)
    c: Horizontal(g3)
    c: Vertical(g4)
    c: Coincident(g5,g4)
    c: Horizontal(g5)
    c: Coincident(g6,g5)
    c: Coincident(g7,g6)
    c: Coincident(g7,g4)
    c: Horizontal(g7)
    c: DistanceY(g6,g-4) = 1.5
    c: DistanceY(g0,g-5) = 1.5
    c: Parallel(g6,g-4)
    c: DistanceY(g-6,g5) = 0
    c: DistanceX(g-5,g0) = 1.5
    c: DistanceX(g2,g4) = 1.5
    c: PointOnObject(g8,g-4)
    c: PointOnObject(g8,g6)
    c: Angle(g8,g-4) = 1.5708
    c: Distance(g8) = 1.5
    c: Distance(g-4,g8) = 4
    c: DistanceX(g3,g3) = 3.2
    c: DistanceY(g2,g2) = 6.7
FEATURE [PartDesign::Pocket] Pocket046
  BaseFeature = -> Pad087
  Direction = (1,0,0)
  Length = 2
  Length2 = 5
  Profile = -> Sketch116
  ReferenceAxis = -> Sketch116 [N_Axis]
  Refine = true
  Suppressed = false
  Type = 0
FEATURE [Sketcher::SketchObject] Sketch117
  ArcFitTolerance = 1e-06
  AttachmentSupport = -> [Pocket046]
  ExternalGeometry = -> [Pocket046]
  FullyConstrained = true
  MakeInternals = false
  MapMode = 5
  Placement = pos=(22.28,0,0) rot=(0.57735,-0.57735,-0.57735;2.0944rad)
  sketch-geometry (6):
    g0: ArcOfCircle CenterX=-38.86 CenterY=13.65 CenterZ=0 NormalX=0 NormalY=0 NormalZ=1 AngleXU=0 Radius=3.25 StartAngle=0.394791 EndAngle=2.7468
    g1: LineSegment [constr] StartX=-38.86 StartY=16.9 StartZ=0 EndX=-42.95 EndY=16.9 EndZ=0
    g2: LineSegment [constr] StartX=-42.95 StartY=16.9 StartZ=0 EndX=-42.95 EndY=11.9 EndZ=0
    g3: LineSegment StartX=-41.86 StartY=14.9 StartZ=0 EndX=-42.95 EndY=11.9 EndZ=0
    g4: LineSegment StartX=-35.86 StartY=14.9 StartZ=0 EndX=-35.05 EndY=11.9 EndZ=0
    g5: LineSegment StartX=-35.05 StartY=11.9 StartZ=0 EndX=-42.95 EndY=11.9 EndZ=0
  constraints (17):
    c: Tangent(g1,g0) = -1.5708
    c: Horizontal(g1)
    c: Coincident(g2,g1)
    c: Vertical(g2)
    c: Coincident(g3,g0)
    c: Coincident(g3,g-3)
    c: Coincident(g4,g0)
    c: Coincident(g4,g-3)
    c: Coincident(g2,g3)
    c: Radius(g0) = 3.25
    c: Coincident(g5,g4)
    c: Coincident(g5,g2)
    c: DistanceY(g2,g2) = 5
    c: DistanceX(g2,g4) = 7.9
    c: DistanceX(g1,g1) = 4.09
    c: DistanceY(g0,g0) = 0
    c: DistanceY(g4,g0) = 3
FEATURE [PartDesign::Pad] Pad088
  BaseFeature = -> Pocket046
  Direction = (-1,0,0)
  Length = 3
  Length2 = 10
  Profile = -> Sketch117
  ReferenceAxis = -> Sketch117 [N_Axis]
  Refine = true
  Reversed = true
  Suppressed = false
  Type = 0
FEATURE [PartDesign::Pad] Pad089
  BaseFeature = -> Pad088
  Direction = (-1,0,0)
  Length = 11.35
  Length2 = 10
  Profile = -> Sketch117
  ReferenceAxis = -> Sketch117 [N_Axis]
  Refine = true
  Suppressed = false
  Type = 0
FEATURE [Sketcher::SketchObject] Sketch118
  ArcFitTolerance = 1e-06
  AttachmentSupport = -> [Pad089]
  ExternalGeometry = -> [Pad089]
  FullyConstrained = true
  MakeInternals = false
  MapMode = 5
  Placement = pos=(0,42.95,0) rot=(0,0.707107,0.707107;3.14159rad)
  sketch-geometry (4):
    g0: LineSegment StartX=-22.28 StartY=11.9 StartZ=0 EndX=-13.93 EndY=11.9 EndZ=0
    g1: LineSegment StartX=-13.93 StartY=11.9 StartZ=0 EndX=-13.93 EndY=16.9 EndZ=0
    g2: LineSegment StartX=-13.93 StartY=16.9 StartZ=0 EndX=-22.28 EndY=16.9 EndZ=0
    g3: LineSegment StartX=-22.28 StartY=16.9 StartZ=0 EndX=-22.28 EndY=11.9 EndZ=0
  constraints (10):
    c: Coincident(g0,g1)
    c: Coincident(g1,g2)
    c: Coincident(g2,g3)
    c: Coincident(g3,g0)
    c: Horizontal(g2)
    c: Vertical(g1)
    c: Vertical(g3)
    c: Coincident(g0,g-3)
    c: Coincident(g0,g-4)
    c: DistanceY(g3,g3) = 5
FEATURE [PartDesign::Pocket] Pocket047
  BaseFeature = -> Pad089
  Direction = (0,-1,2e-16)
  Length = 9
  Length2 = 5
  Profile = -> Sketch118
  ReferenceAxis = -> Sketch118 [N_Axis]
  Refine = true
  Suppressed = false
  Type = 0
FEATURE [PartDesign::Body] Body008  label="Rear_Cab"
  AllowCompound = false
  Group = -> [Binder003,Sketch097,Pad068,Pad069,Sketch098,Pad070,Sketch099,Pad071,Sketch100,Pad072,Sketch101,Pad073,Sketch102,Pad074,Pocket042,Sketch103,Pad075,Sketch106,Pad077,Sketch107,Pocket044,Sketch108,Pad078,Sketch109,Pad079,Sketch110,Pad080,Pad081,Sketch111,Pad082,Pad083,Sketch112,Pad084,Sketch113,Pad085,Sketch114,Pad086,Sketch115,Pad087,Sketch116,Pocket046,Sketch117,Pad088,Pad089,Sketch118,Pocket047,+24 more]
  Origin = -> Origin008
  Tip = -> Fillet005
COMPONENT P9 — recipe-attached ("Rear_Windows", modeled in this document).
Construction recipe (the document's own serialized feature program — sketch geometry with constraints, then the solid features built on it; lengths are millimeters unless a unit is written):

FEATURE [PartDesign::SubShapeBinder] Binder004
  BindCopyOnChange = 0
  BindMode = 2
  ClaimChildren = false
  Context = -> Body009 [Binder004.]
  Fuse = false
  MakeFace = true
  OffsetFill = false
  OffsetIntersection = false
  OffsetJoinType = 0
  OffsetOpenResult = false
  PartialLoad = false
  Refine = true
  Relative = true
  _Version = 2
FEATURE [Sketcher::SketchObject] Sketch129
  ArcFitTolerance = 1e-06
  AttachmentSupport = -> [Binder004]
  ExternalGeometry = -> [Binder004]
  FullyConstrained = true
  MakeInternals = false
  MapMode = 5
  Placement = pos=(8.5,0,0) rot=(0.57735,-0.57735,-0.57735;2.0944rad)
  sketch-geometry (6):
    g0: LineSegment StartX=-31.7 StartY=21.35 StartZ=0 EndX=-20.3093 EndY=21.35 EndZ=0
    g1: LineSegment StartX=-31.7 StartY=21.35 StartZ=0 EndX=-31.7 EndY=10.45 EndZ=0
    g2: LineSegment StartX=-17.3 StartY=10.45 StartZ=0 EndX=-31.7 EndY=10.45 EndZ=0
    g3: LineSegment StartX=-20.3093 StartY=21.35 StartZ=0 EndX=-17.3 EndY=11.8922 EndZ=0
    g4: LineSegment StartX=-17.3 StartY=11.8922 StartZ=0 EndX=-17.3 EndY=10.45 EndZ=0
    g5: LineSegment [constr] StartX=-19.6663 StartY=19.4941 StartZ=0 EndX=-19.714 EndY=19.479 EndZ=0
  constraints (19):
    c: Horizontal(g0)
    c: Coincident(g1,g0)
    c: Vertical(g1)
    c: Coincident(g2,g1)
    c: Horizontal(g2)
    c: Coincident(g3,g0)
    c: Coincident(g4,g3)
    c: Coincident(g4,g2)
    c: DistanceX(g-5,g1) = 0.05
    c: DistanceX(g3,g-7) = 0.05
    c: DistanceY(g-5,g1) = 0.05
    c: DistanceY(g0,g-4) = 0.05
    c: Vertical(g4)
    c: Parallel(g-6,g3)
    c: PointOnObject(g5,g-6)
    c: PointOnObject(g5,g3)
    c: Angle(g5,g-6) = 1.5708
    c: Distance(g5) = 0.05
    c: Distance(g5,g-6) = 2
FEATURE [PartDesign::Pad] Pad098
  Direction = (-1,0,0)
  Length = 1.5
  Length2 = 10
  Profile = -> Sketch129
  ReferenceAxis = -> Sketch129 [N_Axis]
  Refine = true
  Suppressed = false
  Type = 0
FEATURE [Sketcher::SketchObject] Sketch130
  ArcFitTolerance = 1e-06
  AttachmentSupport = -> [Pad098]
  ExternalGeometry = -> [Pad098]
  FullyConstrained = true
  MakeInternals = false
  MapMode = 5
  Placement = pos=(7,0,0) rot=(0.57735,-0.57735,-0.57735;2.0944rad)
  sketch-geometry (11):
    g0: LineSegment StartX=-31.7 StartY=21.35 StartZ=0 EndX=-20.3093 EndY=21.35 EndZ=0
    g1: LineSegment StartX=-20.3093 StartY=21.35 StartZ=0 EndX=-17.3 EndY=11.8922 EndZ=0
    g2: LineSegment StartX=-17.3 StartY=11.8922 StartZ=0 EndX=-17.3 EndY=10.45 EndZ=0
    g3: LineSegment StartX=-17.3 StartY=10.45 StartZ=0 EndX=-18.8 EndY=10.45 EndZ=0
    g4: LineSegment StartX=-18.8 StartY=10.45 StartZ=0 EndX=-18.8 EndY=11.6594 EndZ=0
    g5: LineSegment StartX=-18.8 StartY=11.6594 StartZ=0 EndX=-21.4061 EndY=19.85 EndZ=0
    g6: LineSegment StartX=-21.4061 StartY=19.85 StartZ=0 EndX=-30.2 EndY=19.85 EndZ=0
    g7: LineSegment StartX=-30.2 StartY=19.85 StartZ=0 EndX=-30.2 EndY=10.45 EndZ=0
    g8: LineSegment StartX=-30.2 StartY=10.45 StartZ=0 EndX=-31.7 EndY=10.45 EndZ=0
    g9: LineSegment StartX=-31.7 StartY=21.35 StartZ=0 EndX=-31.7 EndY=10.45 EndZ=0
    g10: LineSegment [constr] StartX=-19.0671 StartY=17.446 StartZ=0 EndX=-20.4965 EndY=16.9912 EndZ=0
  constraints (29):
    c: Coincident(g0,g-6)
    c: Coincident(g0,g-5)
    c: Coincident(g1,g0)
    c: Coincident(g1,g-3)
    c: Coincident(g2,g1)
    c: Coincident(g2,g-7)
    c: Coincident(g3,g2)
    c: PointOnObject(g3,g-7)
    c: Coincident(g4,g3)
    c: Vertical(g4)
    c: Coincident(g5,g4)
    c: Coincident(g6,g5)
    c: Horizontal(g6)
    c: Coincident(g7,g6)
    c: PointOnObject(g7,g-7)
    c: Vertical(g7)
    c: Coincident(g8,g7)
    c: Coincident(g8,g-7)
    c: DistanceX(g8,g8) = 1.5
    c: DistanceX(g3,g3) = 1.5
    c: DistanceY(g6,g0) = 1.5
    c: Coincident(g9,g0)
    c: Coincident(g9,g8)
    c: Parallel(g1,g5)
    c: PointOnObject(g10,g1)
    c: PointOnObject(g10,g5)
    c: Angle(g10,g1) = 1.5708
    c: Distance(g10) = 1.5
    c: Distance(g10,g5) = 3
FEATURE [PartDesign::Pad] Pad099
  BaseFeature = -> Pad098
  Direction = (-1,0,0)
  Length = 5.4
  Length2 = 10
  Profile = -> Sketch130
  ReferenceAxis = -> Sketch130 [N_Axis]
  Refine = true
  Suppressed = false
  Type = 0
FEATURE [Sketcher::SketchObject] Sketch131
  ArcFitTolerance = 1e-06
  AttachmentSupport = -> [Pad099]
  ExternalGeometry = -> [Pad099]
  FullyConstrained = true
  MakeInternals = false
  MapMode = 5
  Placement = pos=(1.6,0,0) rot=(0.57735,-0.57735,-0.57735;2.0944rad)
  sketch-geometry (5):
    g0: LineSegment StartX=-30.2 StartY=19.85 StartZ=0 EndX=-30.2 EndY=10.45 EndZ=0
    g1: LineSegment StartX=-30.2 StartY=19.85 StartZ=0 EndX=-21.4061 EndY=19.85 EndZ=0
    g2: LineSegment StartX=-21.4061 StartY=19.85 StartZ=0 EndX=-18.8 EndY=11.6594 EndZ=0
    g3: LineSegment StartX=-18.8 StartY=11.6594 StartZ=0 EndX=-18.8 EndY=10.45 EndZ=0
    g4: LineSegment StartX=-18.8 StartY=10.45 StartZ=0 EndX=-30.2 EndY=10.45 EndZ=0
  constraints (10):
    c: Coincident(g0,g-7)
    c: Coincident(g0,g-7)
    c: Coincident(g1,g0)
    c: Coincident(g1,g-4)
    c: Coincident(g2,g1)
    c: Coincident(g2,g-6)
    c: Coincident(g3,g2)
    c: Coincident(g3,g-6)
    c: Coincident(g4,g3)
    c: Coincident(g4,g0)
FEATURE [PartDesign::Pad] Pad100
  BaseFeature = -> Pad099
  Direction = (-1,0,0)
  Length = 1.5
  Length2 = 10
  Profile = -> Sketch131
  ReferenceAxis = -> Sketch131 [N_Axis]
  Refine = true
  Reversed = true
  Suppressed = false
  Type = 0
FEATURE [PartDesign::Pad] Pad240
  BaseFeature = -> Pad100
  Direction = (0,0,-1)
  Length = 6.95
  Length2 = 10
  Profile = -> Pad100 [Face6]
  Refine = true
  Suppressed = false
  Type = 0
FEATURE [Sketcher::SketchObject] Sketch341
  ArcFitTolerance = 1e-06
  AttachmentSupport = -> [Pad240]
  ExternalGeometry = -> [Pad240]
  FullyConstrained = true
  MakeInternals = false
  MapMode = 5
  Placement = pos=(0,0,3.5) rot=(1,0,0;3.14159rad)
  sketch-geometry (6):
    g0: LineSegment StartX=1.6 StartY=-31.7 StartZ=0 EndX=7 EndY=-31.7 EndZ=0
    g1: LineSegment StartX=7 StartY=-31.7 StartZ=0 EndX=7 EndY=-30.2 EndZ=0
    g2: LineSegment StartX=7 StartY=-30.2 StartZ=0 EndX=3.1 EndY=-30.2 EndZ=0
    g3: LineSegment StartX=3.1 StartY=-30.2 StartZ=0 EndX=3.1 EndY=-27.2 EndZ=0
    g4: LineSegment StartX=3.1 StartY=-27.2 StartZ=0 EndX=1.6 EndY=-27.2 EndZ=0
    g5: LineSegment StartX=1.6 StartY=-27.2 StartZ=0 EndX=1.6 EndY=-31.7 EndZ=0
  constraints (15):
    c: Coincident(g0,g1)
    c: Coincident(g1,g2)
    c: Vertical(g1)
    c: Horizontal(g0)
    c: Coincident(g1,g-3)
    c: Coincident(g3,g2)
    c: PointOnObject(g3,g-5)
    c: Coincident(g4,g3)
    c: PointOnObject(g4,g-6)
    c: Horizontal(g4)
    c: Coincident(g5,g4)
    c: Coincident(g5,g-6)
    c: Coincident(g0,g5)
    c: Coincident(g2,g-5)
    c: DistanceY(g3,g3) = 3
FEATURE [PartDesign::Pocket] Pocket160
  BaseFeature = -> Pad240
  Direction = (0,0,1)
  Length = 6.9
  Length2 = 5
  Profile = -> Sketch341
  ReferenceAxis = -> Sketch341 [N_Axis]
  Refine = true
  Suppressed = false
  Type = 0
FEATURE [PartDesign::Body] Body009  label="Rear_Windows"
  AllowCompound = false
  Group = -> [Binder004,Sketch129,Pad098,Sketch130,Pad099,Sketch131,Pad100,Pad240,Sketch341,Pocket160]
  Origin = -> Origin009
  Tip = -> Pocket160
COMPONENT P10 — recipe-attached ("Front_Torso", modeled in this document).
Construction recipe (the document's own serialized feature program — sketch geometry with constraints, then the solid features built on it; lengths are millimeters unless a unit is written):

FEATURE [PartDesign::SubShapeBinder] Binder005
  BindCopyOnChange = 0
  BindMode = 2
  ClaimChildren = false
  Context = -> Body010 [Binder005.]
  Fuse = false
  MakeFace = true
  OffsetFill = false
  OffsetIntersection = false
  OffsetJoinType = 0
  OffsetOpenResult = false
  PartialLoad = false
  Refine = true
  Relative = true
  _Version = 2
FEATURE [Sketcher::SketchObject] Sketch133
  ArcFitTolerance = 1e-06
  AttachmentSupport = -> [Binder005]
  ExternalGeometry = -> [Binder005]
  FullyConstrained = true
  MakeInternals = false
  MapMode = 5
  Placement = pos=(0,0,-4) rot=(1,0,0;3.14159rad)
  sketch-geometry (22):
    g0: LineSegment StartX=7.05 StartY=0 StartZ=0 EndX=28.95 EndY=0 EndZ=0
    g1: LineSegment StartX=28.95 StartY=0 StartZ=0 EndX=28.95 EndY=-10 EndZ=0
    g2: LineSegment StartX=28.95 StartY=-10 StartZ=0 EndX=27 EndY=-10 EndZ=0
    g3: LineSegment StartX=27 StartY=-10 StartZ=0 EndX=27.4 EndY=-17.2 EndZ=0
    g4: LineSegment StartX=27.4 StartY=-17.2 StartZ=0 EndX=29 EndY=-17.2 EndZ=0
    g5: LineSegment StartX=29 StartY=-17.2 StartZ=0 EndX=29 EndY=-26.3 EndZ=0
    g6: LineSegment StartX=29 StartY=-26.3 StartZ=0 EndX=27 EndY=-26.3 EndZ=0
    g7: LineSegment StartX=27 StartY=-26.3 StartZ=0 EndX=27 EndY=-19.2 EndZ=0
    g8: LineSegment StartX=27 StartY=-19.2 StartZ=0 EndX=25 EndY=-19.2 EndZ=0
    g9: LineSegment StartX=25 StartY=-19.2 StartZ=0 EndX=25 EndY=-3 EndZ=0
    g10: LineSegment StartX=25 StartY=-3 StartZ=0 EndX=21.127 EndY=-2 EndZ=0
    g11: LineSegment StartX=21.127 StartY=-2 StartZ=0 EndX=14.873 EndY=-2 EndZ=0
    g12: LineSegment StartX=14.873 StartY=-2 StartZ=0 EndX=11 EndY=-3 EndZ=0
    g13: LineSegment StartX=11 StartY=-3 StartZ=0 EndX=11 EndY=-19.2 EndZ=0
    g14: LineSegment StartX=11 StartY=-19.2 StartZ=0 EndX=9 EndY=-19.2 EndZ=0
    g15: LineSegment StartX=9 StartY=-19.2 StartZ=0 EndX=9 EndY=-26.3 EndZ=0
    g16: LineSegment StartX=9 StartY=-26.3 StartZ=0 EndX=7 EndY=-26.3 EndZ=0
    g17: LineSegment StartX=7 StartY=-26.3 StartZ=0 EndX=7 EndY=-17.2 EndZ=0
    g18: LineSegment StartX=7 StartY=-17.2 StartZ=0 EndX=8.6 EndY=-17.2 EndZ=0
    g19: LineSegment StartX=8.6 StartY=-17.2 StartZ=0 EndX=9 EndY=-10 EndZ=0
    g20: LineSegment StartX=9 StartY=-10 StartZ=0 EndX=7.05 EndY=-10 EndZ=0
    g21: LineSegment StartX=7.05 StartY=-10 StartZ=0 EndX=7.05 EndY=0 EndZ=0
  constraints (62):
    c: PointOnObject(g0,g-5)
    c: PointOnObject(g0,g-5)
    c: Coincident(g1,g0)
    c: Vertical(g1)
    c: Coincident(g2,g1)
    c: Coincident(g3,g2)
    c: Coincident(g4,g3)
    c: Coincident(g5,g4)
    c: Coincident(g6,g5)
    c: Coincident(g7,g6)
    c: Vertical(g7)
    c: Coincident(g8,g7)
    c: Horizontal(g8)
    c: Coincident(g9,g8)
    c: Vertical(g9)
    c: Coincident(g10,g9)
    c: Coincident(g11,g10)
    c: Horizontal(g11)
    c: Coincident(g12,g11)
    c: Coincident(g13,g12)
    c: Coincident(g14,g13)
    c: Horizontal(g14)
    c: Coincident(g15,g14)
    c: Vertical(g15)
    c: Coincident(g16,g15)
    c: Coincident(g17,g16)
    c: Coincident(g18,g17)
    c: Horizontal(g18)
    c: Coincident(g19,g18)
    c: Coincident(g20,g19)
    c: Horizontal(g20)
    c: Coincident(g21,g20)
    c: Coincident(g21,g0)
    c: Vertical(g21)
    c: DistanceX(g-7,g0) = 0.05
    c: DistanceX(g0,g-5) = 0.05
    c: DistanceY(g11,g-7) = 2
    c: DistanceX(g9,g0) = 3.95
    c: DistanceX(g0,g12) = 3.95
    c: DistanceX(g20,g20) = 1.95
    c: DistanceX(g2,g2) = 1.95
    c: DistanceY(g12,g11) = 1
    c: DistanceY(g9,g10) = 1
    c: Distance(g12) = 4
    c: Distance(g10) = 4
    c: DistanceX(g18,g18) = 1.6
    c: PointOnObject(g17,g-6)
    c: PointOnObject(g4,g-3)
    c: Horizontal(g4)
    c: DistanceX(g4,g4) = 1.6
    c: DistanceY(g3,g2) = 7.2
    c: Horizontal(g2)
    c: DistanceY(g18,g19) = 7.2
    c: DistanceY(g21,g21) = 10
    c: DistanceY(g1,g1) = 10
    c: Coincident(g16,g-9)
    c: Coincident(g15,g-9)
    c: Coincident(g5,g-3)
    c: Coincident(g6,g-10)
    c: Vertical(g13)
    c: DistanceY(g13,g18) = 2
    c: DistanceY(g8,g3) = 2
FEATURE [PartDesign::Pad] Pad101
  Direction = (0,0,-1)
  Length = 2
  Length2 = 10
  Profile = -> Sketch133
  ReferenceAxis = -> Sketch133 [N_Axis]
  Refine = true
  Suppressed = false
  Type = 0
FEATURE [Sketcher::SketchObject] Sketch134
  ArcFitTolerance = 1e-06
  AttachmentSupport = -> [Pad101]
  ExternalGeometry = -> [Pad101]
  FullyConstrained = true
  MakeInternals = false
  MapMode = 5
  Placement = pos=(0,0,-6) rot=(1,0,0;3.14159rad)
  sketch-geometry (12):
    g0: LineSegment StartX=7.05 StartY=0 StartZ=0 EndX=28.95 EndY=0 EndZ=0
    g1: LineSegment StartX=28.95 StartY=0 StartZ=0 EndX=28.95 EndY=-10 EndZ=0
    g2: LineSegment StartX=28.95 StartY=-10 StartZ=0 EndX=27 EndY=-10 EndZ=0
    g3: LineSegment StartX=27 StartY=-10 StartZ=0 EndX=27.4 EndY=-17.2 EndZ=0
    g4: LineSegment StartX=27.4 StartY=-17.2 StartZ=0 EndX=29 EndY=-17.2 EndZ=0
    g5: LineSegment StartX=29 StartY=-17.2 StartZ=0 EndX=29 EndY=-19.2 EndZ=0
    g6: LineSegment StartX=29 StartY=-19.2 StartZ=0 EndX=7 EndY=-19.2 EndZ=0
    g7: LineSegment StartX=7 StartY=-19.2 StartZ=0 EndX=7 EndY=-17.2 EndZ=0
    g8: LineSegment StartX=7 StartY=-17.2 StartZ=0 EndX=8.6 EndY=-17.2 EndZ=0
    g9: LineSegment StartX=8.6 StartY=-17.2 StartZ=0 EndX=9 EndY=-10 EndZ=0
    g10: LineSegment StartX=9 StartY=-10 StartZ=0 EndX=7.05 EndY=-10 EndZ=0
    g11: LineSegment StartX=7.05 StartY=-10 StartZ=0 EndX=7.05 EndY=0 EndZ=0
  constraints (26):
    c: Coincident(g0,g-5)
    c: Coincident(g0,g-4)
    c: Coincident(g1,g0)
    c: Coincident(g1,g-3)
    c: Coincident(g2,g1)
    c: Coincident(g2,g-14)
    c: Coincident(g3,g2)
    c: Coincident(g3,g-14)
    c: Coincident(g4,g3)
    c: Coincident(g4,g-16)
    c: Coincident(g5,g4)
    c: PointOnObject(g5,g-16)
    c: Coincident(g6,g5)
    c: PointOnObject(g6,g-12)
    c: Horizontal(g6)
    c: PointOnObject(g-11,g6)
    c: Coincident(g7,g6)
    c: Coincident(g7,g-12)
    c: Coincident(g8,g7)
    c: Coincident(g8,g-7)
    c: Coincident(g9,g8)
    c: Coincident(g9,g-7)
    c: Coincident(g10,g9)
    c: Coincident(g10,g-6)
    c: Coincident(g11,g10)
    c: Coincident(g11,g0)
FEATURE [PartDesign::Pad] Pad102
  BaseFeature = -> Pad101
  Direction = (0,0,-1)
  Length = 2
  Length2 = 10
  Profile = -> Sketch134
  ReferenceAxis = -> Sketch134 [N_Axis]
  Refine = true
  Suppressed = false
  Type = 0
FEATURE [Sketcher::SketchObject] Sketch135
  ArcFitTolerance = 1e-06
  AttachmentSupport = -> [Pad102]
  ExternalGeometry = -> [Pad102]
  FullyConstrained = true
  MakeInternals = false
  MapMode = 5
  Placement = pos=(0,0,-8) rot=(1,0,0;3.14159rad)
  sketch-geometry (4):
    g0: LineSegment StartX=7 StartY=-19.2 StartZ=0 EndX=29 EndY=-19.2 EndZ=0
    g1: LineSegment StartX=29 StartY=-19.2 StartZ=0 EndX=29 EndY=-36.4 EndZ=0
    g2: LineSegment StartX=29 StartY=-36.4 StartZ=0 EndX=7 EndY=-36.4 EndZ=0
    g3: LineSegment StartX=7 StartY=-36.4 StartZ=0 EndX=7 EndY=-19.2 EndZ=0
  constraints (10):
    c: Coincident(g0,g-3)
    c: Coincident(g0,g-3)
    c: Coincident(g1,g0)
    c: Vertical(g1)
    c: Coincident(g2,g1)
    c: Horizontal(g2)
    c: Coincident(g3,g2)
    c: Coincident(g3,g0)
    c: Vertical(g3)
    c: DistanceY(g3,g3) = 17.2
FEATURE [PartDesign::Pad] Pad103
  BaseFeature = -> Pad102
  Direction = (0,0,-1)
  Length = 2
  Length2 = 10
  Profile = -> Pad102 [Face13,Face15]
  Refine = true
  Suppressed = false
  Type = 0
FEATURE [PartDesign::Pad] Pad104
  BaseFeature = -> Pad103
  Direction = (0,0,-1)
  Length = 2
  Length2 = 10
  Profile = -> Sketch135
  ReferenceAxis = -> Sketch135 [N_Axis]
  Refine = true
  Suppressed = false
  Type = 0
FEATURE [Sketcher::SketchObject] Sketch136
  ArcFitTolerance = 1e-06
  AttachmentSupport = -> [Pad104]
  ExternalGeometry = -> [Pad104]
  FullyConstrained = true
  MakeInternals = false
  MapMode = 5
  Placement = pos=(7,0,0) rot=(0.57735,-0.57735,-0.57735;2.0944rad)
  sketch-geometry (7):
    g0: LineSegment StartX=-36.4 StartY=-10 StartZ=0 EndX=-41.35 EndY=-7.14212 EndZ=0
    g1: LineSegment StartX=-41.35 StartY=-7.14212 StartZ=0 EndX=-41.35 EndY=-4 EndZ=0
    g2: LineSegment StartX=-41.35 StartY=-4 StartZ=0 EndX=-34.4 EndY=-4 EndZ=0
    g3: LineSegment StartX=-36.4 StartY=-8 StartZ=0 EndX=-36.4 EndY=-10 EndZ=0
    g4: LineSegment [constr] StartX=-36.4 StartY=-10 StartZ=0 EndX=-41.35 EndY=-10 EndZ=0
    g5: LineSegment StartX=-36.4 StartY=-8 StartZ=0 EndX=-34.4 EndY=-8 EndZ=0
    g6: LineSegment StartX=-34.4 StartY=-8 StartZ=0 EndX=-34.4 EndY=-4 EndZ=0
  constraints (19):
    c: Coincident(g0,g-4)
    c: Coincident(g1,g0)
    c: Vertical(g1)
    c: Coincident(g2,g1)
    c: Horizontal(g2)
    c: Coincident(g3,g0)
    c: Angle(g3,g0) = 1.0472
    c: Coincident(g4,g0)
    c: Horizontal(g4)
    c: DistanceX(g4,g4) = 4.95
    c: DistanceX(g4,g0) = 0
    c: Coincident(g5,g3)
    c: PointOnObject(g5,g-3)
    c: Coincident(g6,g5)
    c: Vertical(g6)
    c: Coincident(g2,g6)
    c: DistanceY(g6,g6) = 4
    c: DistanceX(g2,g2) = 6.95
    c: Coincident(g3,g-4)
FEATURE [PartDesign::Pad] Pad105
  BaseFeature = -> Pad104
  Direction = (-1,0,0)
  Length = 22
  Length2 = 10
  Profile = -> Sketch136
  ReferenceAxis = -> Sketch136 [N_Axis]
  Refine = true
  Reversed = true
  Suppressed = false
  Type = 0
FEATURE [Sketcher::SketchObject] Sketch137
  ArcFitTolerance = 1e-06
  AttachmentSupport = -> [Pad105]
  ExternalGeometry = -> [Pad105]
  FullyConstrained = true
  MakeInternals = false
  MapMode = 5
  Placement = pos=(0,0,-8) rot=(1,0,0;3.14159rad)
  sketch-geometry (4):
    g0: LineSegment StartX=23.25 StartY=-10 StartZ=0 EndX=23.25 EndY=8 EndZ=0
    g1: LineSegment StartX=23.25 StartY=8 StartZ=0 EndX=12.75 EndY=8 EndZ=0
    g2: LineSegment StartX=12.75 StartY=8 StartZ=0 EndX=12.75 EndY=-10 EndZ=0
    g3: LineSegment StartX=12.75 StartY=-10 StartZ=0 EndX=23.25 EndY=-10 EndZ=0
  constraints (13):
    c: Coincident(g0,g1)
    c: Coincident(g1,g2)
    c: Coincident(g2,g3)
    c: Coincident(g3,g0)
    c: Vertical(g0)
    c: Vertical(g2)
    c: Horizontal(g1)
    c: Horizontal(g3)
    c: DistanceX(g1,g1) = 10.5
    c: DistanceX(g-4,g-3) = 21.9
    c: DistanceX(g-4,g1) = 5.7
    c: DistanceY(g-5,g2) = 0
    c: DistanceY(g0,g0) = 18
FEATURE [PartDesign::Pad] Pad106
  BaseFeature = -> Pad105
  Direction = (0,0,-1)
  Length = 2
  Length2 = 10
  Profile = -> Sketch137
  ReferenceAxis = -> Sketch137 [N_Axis]
  Refine = true
  Suppressed = false
  Type = 0
FEATURE [Sketcher::SketchObject] Sketch138
  ArcFitTolerance = 1e-06
  AttachmentSupport = -> [Pad106]
  ExternalGeometry = -> [Pad106]
  FullyConstrained = true
  MakeInternals = false
  MapMode = 5
  Placement = pos=(0,0,-8) rot=(1,0,0;3.14159rad)
  sketch-geometry (8):
    g0: LineSegment StartX=28.95 StartY=0 StartZ=0 EndX=23.25 EndY=0 EndZ=0
    g1: LineSegment StartX=23.25 StartY=0 StartZ=0 EndX=23.25 EndY=-10 EndZ=0
    g2: LineSegment StartX=23.25 StartY=-10 StartZ=0 EndX=28.95 EndY=-10 EndZ=0
    g3: LineSegment StartX=28.95 StartY=-10 StartZ=0 EndX=28.95 EndY=0 EndZ=0
    g4: LineSegment StartX=7.05 StartY=0 StartZ=0 EndX=7.05 EndY=-10 EndZ=0
    g5: LineSegment StartX=7.05 StartY=-10 StartZ=0 EndX=12.75 EndY=-10 EndZ=0
    g6: LineSegment StartX=12.75 StartY=-10 StartZ=0 EndX=12.75 EndY=0 EndZ=0
    g7: LineSegment StartX=12.75 StartY=0 StartZ=0 EndX=7.05 EndY=0 EndZ=0
  constraints (20):
    c: Coincident(g0,g1)
    c: Coincident(g1,g2)
    c: Coincident(g2,g3)
    c: Coincident(g3,g0)
    c: Horizontal(g0)
    c: Horizontal(g2)
    c: Vertical(g1)
    c: Vertical(g3)
    c: Coincident(g0,g-9)
    c: Coincident(g1,g-10)
    c: Coincident(g4,g5)
    c: Coincident(g5,g6)
    c: Coincident(g6,g7)
    c: Coincident(g7,g4)
    c: Vertical(g4)
    c: Vertical(g6)
    c: Horizontal(g5)
    c: Horizontal(g7)
    c: Coincident(g4,g-5)
    c: Coincident(g5,g-3)
FEATURE [PartDesign::Pad] Pad107
  BaseFeature = -> Pad106
  Direction = (0,0,-1)
  Length = 1
  Length2 = 10
  Profile = -> Sketch138
  ReferenceAxis = -> Sketch138 [N_Axis]
  Refine = true
  Suppressed = false
  Type = 0
FEATURE [Sketcher::SketchObject] Sketch139
  ArcFitTolerance = 1e-06
  AttachmentSupport = -> [Pad107]
  ExternalGeometry = -> [Pad107]
  FullyConstrained = true
  MakeInternals = false
  MapMode = 5
  Placement = pos=(0,0,-10) rot=(1,0,0;3.14159rad)
  sketch-geometry (4):
    g0: LineSegment StartX=13.9 StartY=-36.4 StartZ=0 EndX=13.9 EndY=-41.35 EndZ=0
    g1: LineSegment StartX=13.9 StartY=-41.35 StartZ=0 EndX=22.1 EndY=-41.35 EndZ=0
    g2: LineSegment StartX=22.1 StartY=-41.35 StartZ=0 EndX=22.1 EndY=-36.4 EndZ=0
    g3: LineSegment StartX=22.1 StartY=-36.4 StartZ=0 EndX=13.9 EndY=-36.4 EndZ=0
  constraints (12):
    c: Coincident(g0,g1)
    c: Coincident(g1,g2)
    c: Coincident(g2,g3)
    c: Coincident(g3,g0)
    c: Vertical(g0)
    c: Vertical(g2)
    c: Horizontal(g1)
    c: Horizontal(g3)
    c: DistanceX(g3,g3) = 8.2
    c: PointOnObject(g0,g-3)
    c: PointOnObject(g0,g-4)
    c: DistanceX(g1,g-4) = 6.9
FEATURE [PartDesign::Pocket] Pocket053
  BaseFeature = -> Pad107
  Direction = (0,0,1)
  Length = 6
  Length2 = 5
  Profile = -> Sketch139
  ReferenceAxis = -> Sketch139 [N_Axis]
  Refine = true
  Suppressed = false
  Type = 0
FEATURE [Sketcher::SketchObject] Sketch140
  ArcFitTolerance = 1e-06
  AttachmentSupport = -> [Pocket053]
  ExternalGeometry = -> [Pocket053]
  FullyConstrained = true
  MakeInternals = false
  MapMode = 5
  Placement = pos=(0,0,-4) rot=(0,0,1;0rad)
  sketch-geometry (4):
    g0: LineSegment StartX=13.9 StartY=36.4 StartZ=0 EndX=13.9 EndY=34.4 EndZ=0
    g1: LineSegment StartX=13.9 StartY=34.4 StartZ=0 EndX=22.1 EndY=34.4 EndZ=0
    g2: LineSegment StartX=22.1 StartY=34.4 StartZ=0 EndX=22.1 EndY=36.4 EndZ=0
    g3: LineSegment StartX=22.1 StartY=36.4 StartZ=0 EndX=13.9 EndY=36.4 EndZ=0
  constraints (10):
    c: Coincident(g0,g1)
    c: Coincident(g1,g2)
    c: Coincident(g2,g3)
    c: Coincident(g3,g0)
    c: Vertical(g0)
    c: Vertical(g2)
    c: Horizontal(g1)
    c: Coincident(g0,g-3)
    c: PointOnObject(g1,g-4)
    c: Coincident(g2,g-3)
FEATURE [PartDesign::Pocket] Pocket054
  BaseFeature = -> Pocket053
  Direction = (0,0,-1)
  Length = 4
  Length2 = 5
  Profile = -> Sketch140
  ReferenceAxis = -> Sketch140 [N_Axis]
  Refine = true
  Suppressed = false
  Type = 0
FEATURE [Sketcher::SketchObject] Sketch141
  ArcFitTolerance = 1e-06
  AttachmentSupport = -> [Pocket054]
  ExternalGeometry = -> [Pocket054]
  FullyConstrained = true
  MakeInternals = false
  MapMode = 5
  Placement = pos=(22.1,0,0) rot=(0.57735,-0.57735,-0.57735;2.0944rad)
  sketch-geometry (5):
    g0: LineSegment StartX=-34.4 StartY=-4 StartZ=0 EndX=-39.35 EndY=-4 EndZ=0
    g1: LineSegment StartX=-34.4 StartY=-4 StartZ=0 EndX=-34.4 EndY=-8 EndZ=0
    g2: LineSegment StartX=-34.4 StartY=-8 StartZ=0 EndX=-36.4 EndY=-8 EndZ=0
    g3: LineSegment StartX=-36.4 StartY=-8 StartZ=0 EndX=-39.35 EndY=-6.29682 EndZ=0
    g4: LineSegment StartX=-39.35 StartY=-6.29682 StartZ=0 EndX=-39.35 EndY=-4 EndZ=0
  constraints (13):
    c: Coincident(g0,g-4)
    c: PointOnObject(g0,g-3)
    c: PointOnObject(g1,g0)
    c: Coincident(g1,g-5)
    c: Vertical(g1)
    c: Coincident(g2,g1)
    c: Coincident(g2,g-5)
    c: Coincident(g3,g2)
    c: Coincident(g4,g3)
    c: Coincident(g4,g0)
    c: Parallel(g3,g-6)
    c: Vertical(g4)
    c: DistanceX(g-3,g0) = 2
FEATURE [PartDesign::Pocket] Pocket055
  BaseFeature = -> Pocket054
  Direction = (1,0,0)
  Length = 4.9
  Length2 = 5
  Profile = -> Sketch141
  ReferenceAxis = -> Sketch141 [N_Axis]
  Refine = true
  Suppressed = false
  Type = 0
FEATURE [Sketcher::SketchObject] Sketch142
  ArcFitTolerance = 1e-06
  AttachmentSupport = -> [Pocket055]
  ExternalGeometry = -> [Pocket055]
  FullyConstrained = true
  MakeInternals = false
  MapMode = 5
  Placement = pos=(13.9,0,0) rot=(0.57735,0.57735,0.57735;2.0944rad)
  sketch-geometry (5):
    g0: LineSegment StartX=36.4 StartY=-8 StartZ=0 EndX=34.4 EndY=-8 EndZ=0
    g1: LineSegment StartX=34.4 StartY=-8 StartZ=0 EndX=34.4 EndY=-4 EndZ=0
    g2: LineSegment StartX=34.4 StartY=-4 StartZ=0 EndX=39.35 EndY=-4 EndZ=0
    g3: LineSegment StartX=36.4 StartY=-8 StartZ=0 EndX=39.35 EndY=-6.29682 EndZ=0
    g4: LineSegment StartX=39.35 StartY=-6.29682 StartZ=0 EndX=39.35 EndY=-4 EndZ=0
  constraints (12):
    c: Coincident(g0,g-5)
    c: Coincident(g0,g-5)
    c: Coincident(g1,g0)
    c: Coincident(g1,g-4)
    c: Coincident(g2,g1)
    c: PointOnObject(g2,g-4)
    c: Coincident(g3,g0)
    c: Coincident(g4,g3)
    c: Coincident(g4,g2)
    c: Vertical(g4)
    c: Parallel(g-6,g3)
    c: DistanceX(g2,g-4) = 2
FEATURE [PartDesign::Pocket] Pocket056
  BaseFeature = -> Pocket055
  Direction = (-1,0,0)
  Length = 4.9
  Length2 = 5
  Profile = -> Sketch142
  ReferenceAxis = -> Sketch142 [N_Axis]
  Refine = true
  Suppressed = false
  Type = 0
FEATURE [PartDesign::Pad] Pad108
  BaseFeature = -> Pocket056
  Direction = (0,0,1)
  Length = 2
  Length2 = 10
  Profile = -> Pocket056 [Face4]
  Refine = true
  Suppressed = false
  Type = 0
FEATURE [Sketcher::SketchObject] Sketch143
  ArcFitTolerance = 1e-06
  AttachmentSupport = -> [Pad108]
  ExternalGeometry = -> [Pad108]
  FullyConstrained = true
  MakeInternals = false
  MapMode = 5
  Placement = pos=(12.75,0,0) rot=(0.57735,-0.57735,-0.57735;2.0944rad)
  sketch-geometry (4):
    g0: LineSegment StartX=6 StartY=-6 StartZ=0 EndX=4 EndY=-8 EndZ=0
    g1: LineSegment StartX=4 StartY=-8 StartZ=0 EndX=0 EndY=-8 EndZ=0
    g2: LineSegment StartX=0 StartY=-8 StartZ=0 EndX=0 EndY=-6 EndZ=0
    g3: LineSegment StartX=0 StartY=-6 StartZ=0 EndX=6 EndY=-6 EndZ=0
  constraints (11):
    c: PointOnObject(g0,g-4)
    c: Coincident(g1,g0)
    c: PointOnObject(g1,g-5)
    c: Horizontal(g1)
    c: Coincident(g2,g1)
    c: Coincident(g2,g-4)
    c: Coincident(g3,g2)
    c: DistanceX(g0,g-4) = 2
    c: DistanceY(g2,g2) = 2
    c: Angle(g3,g0) = 0.785398
    c: Coincident(g3,g0)
FEATURE [PartDesign::Pocket] Pocket057
  BaseFeature = -> Pad108
  Direction = (1,0,0)
  Length = 8.5
  Length2 = 5
  Profile = -> Sketch143
  ReferenceAxis = -> Sketch143 [N_Axis]
  Refine = true
  Suppressed = false
  Type = 0
FEATURE [Sketcher::SketchObject] Sketch144
  ArcFitTolerance = 1e-06
  AttachmentSupport = -> [Pocket057]
  ExternalGeometry = -> [Pocket057]
  FullyConstrained = true
  MakeInternals = false
  MapMode = 5
  Placement = pos=(12.75,0,0) rot=(0.57735,-0.57735,-0.57735;2.0944rad)
  sketch-geometry (4):
    g0: LineSegment StartX=6 StartY=-6 StartZ=0 EndX=4 EndY=-8 EndZ=0
    g1: LineSegment StartX=0 StartY=-6 StartZ=0 EndX=6 EndY=-6 EndZ=0
    g2: LineSegment StartX=4 StartY=-8 StartZ=0 EndX=0 EndY=-8 EndZ=0
    g3: LineSegment StartX=0 StartY=-8 StartZ=0 EndX=0 EndY=-6 EndZ=0
  constraints (8):
    c: Coincident(g0,g-3)
    c: Coincident(g0,g-4)
    c: Coincident(g2,g0)
    c: Coincident(g2,g-6)
    c: Coincident(g3,g2)
    c: Coincident(g3,g1)
    c: Coincident(g1,g-6)
    c: Coincident(g1,g0)
FEATURE [PartDesign::Pad] Pad109
  BaseFeature = -> Pocket057
  Direction = (-1,0,0)
  Length = 2
  Length2 = 10
  Profile = -> Sketch144
  ReferenceAxis = -> Sketch144 [N_Axis]
  Refine = true
  Reversed = true
  Suppressed = false
  Type = 0
FEATURE [Sketcher::SketchObject] Sketch145
  ArcFitTolerance = 1e-06
  AttachmentSupport = -> [Pad109]
  ExternalGeometry = -> [Pad109]
  FullyConstrained = true
  MakeInternals = false
  MapMode = 5
  Placement = pos=(0,0,-8) rot=(0,0,1;0rad)
  sketch-geometry (16):
    g0: LineSegment StartX=7 StartY=34.4 StartZ=0 EndX=7 EndY=32.4 EndZ=0
    g1: LineSegment StartX=7 StartY=32.4 StartZ=0 EndX=16.5 EndY=32.4 EndZ=0
    g2: LineSegment StartX=16.5 StartY=32.4 StartZ=0 EndX=16.5 EndY=34.4 EndZ=0
    g3: LineSegment StartX=16.5 StartY=34.4 StartZ=0 EndX=7 EndY=34.4 EndZ=0
    g4: LineSegment StartX=29 StartY=34.4 StartZ=0 EndX=19.5 EndY=34.4 EndZ=0
    g5: LineSegment StartX=19.5 StartY=34.4 StartZ=0 EndX=19.5 EndY=32.4 EndZ=0
    g6: LineSegment StartX=19.5 StartY=32.4 StartZ=0 EndX=29 EndY=32.4 EndZ=0
    g7: LineSegment StartX=29 StartY=32.4 StartZ=0 EndX=29 EndY=34.4 EndZ=0
    g8: LineSegment StartX=7 StartY=26.3 StartZ=0 EndX=16.5 EndY=26.3 EndZ=0
    g9: LineSegment StartX=16.5 StartY=26.3 StartZ=0 EndX=16.5 EndY=28.3 EndZ=0
    g10: LineSegment StartX=16.5 StartY=28.3 StartZ=0 EndX=7 EndY=28.3 EndZ=0
    g11: LineSegment StartX=7 StartY=28.3 StartZ=0 EndX=7 EndY=26.3 EndZ=0
    g12: LineSegment StartX=29 StartY=26.3 StartZ=0 EndX=29 EndY=28.3 EndZ=0
    g13: LineSegment StartX=29 StartY=28.3 StartZ=0 EndX=19.5 EndY=28.3 EndZ=0
    g14: LineSegment StartX=19.5 StartY=28.3 StartZ=0 EndX=19.5 EndY=26.3 EndZ=0
    g15: LineSegment StartX=19.5 StartY=26.3 StartZ=0 EndX=29 EndY=26.3 EndZ=0
  constraints (44):
    c: Coincident(g0,g1)
    c: Coincident(g1,g2)
    c: Coincident(g2,g3)
    c: Coincident(g3,g0)
    c: Vertical(g0)
    c: Vertical(g2)
    c: Horizontal(g1)
    c: Horizontal(g3)
    c: Coincident(g0,g-5)
    c: Coincident(g4,g5)
    c: Coincident(g5,g6)
    c: Coincident(g6,g7)
    c: Coincident(g7,g4)
    c: Horizontal(g4)
    c: Horizontal(g6)
    c: Vertical(g5)
    c: Vertical(g7)
    c: Coincident(g4,g-4)
    c: Coincident(g8,g9)
    c: Coincident(g9,g10)
    c: Coincident(g10,g11)
    c: Coincident(g11,g8)
    c: Horizontal(g8)
    c: Horizontal(g10)
    c: Vertical(g9)
    c: Vertical(g11)
    c: Coincident(g8,g-6)
    c: Coincident(g12,g13)
    c: Coincident(g13,g14)
    c: Coincident(g14,g15)
    c: Coincident(g15,g12)
    c: Vertical(g12)
    c: Vertical(g14)
    c: Horizontal(g13)
    c: Horizontal(g15)
    c: Coincident(g12,g-3)
    c: DistanceX(g1,g1) = 9.5
    c: DistanceX(g10,g10) = 9.5
    c: DistanceX(g13,g13) = 9.5
    c: DistanceX(g6,g6) = 9.5
    c: DistanceY(g5,g5) = 2
    c: DistanceY(g2,g2) = 2
    c: DistanceY(g9,g9) = 2
    c: DistanceY(g14,g14) = 2
FEATURE [PartDesign::Pad] Pad110
  BaseFeature = -> Pad109
  Direction = (0,0,1)
  Length = 0.7
  Length2 = 10
  Profile = -> Sketch145
  ReferenceAxis = -> Sketch145 [N_Axis]
  Refine = true
  Suppressed = false
  Type = 0
FEATURE [Sketcher::SketchObject] Sketch146
  ArcFitTolerance = 1e-06
  AttachmentSupport = -> [Pad110]
  ExternalGeometry = -> [Pad110]
  FullyConstrained = true
  MakeInternals = false
  MapMode = 5
  Placement = pos=(0,0,-8) rot=(0,0,1;0rad)
  sketch-geometry (1):
    g0: Circle CenterX=18 CenterY=20.4 CenterZ=0 NormalX=0 NormalY=0 NormalZ=1 AngleXU=0 Radius=3.5
  constraints (4):
    c: DistanceX(g-3,g-3) = 14
    c: DistanceX(g0,g-3) = 7
    c: Diameter(g0) = 7
    c: DistanceY(g0,g-6) = 16
FEATURE [PartDesign::Pad] Pad111
  BaseFeature = -> Pad110
  Direction = (0,0,1)
  Length = 3
  Length2 = 10
  Profile = -> Sketch146
  ReferenceAxis = -> Sketch146 [N_Axis]
  Refine = true
  Suppressed = false
  Type = 0
FEATURE [Sketcher::SketchObject] Sketch147
  ArcFitTolerance = 1e-06
  AttachmentSupport = -> [Pad111]
  ExternalGeometry = -> [Pad111]
  FullyConstrained = true
  MakeInternals = false
  MapMode = 5
  Placement = pos=(0,0,-5) rot=(0,0,1;0rad)
  sketch-geometry (1):
    g0: Circle CenterX=18 CenterY=20.4 CenterZ=0 NormalX=0 NormalY=0 NormalZ=1 AngleXU=0 Radius=2.5
  constraints (2):
    c: Coincident(g0,g-3)
    c: Radius(g0) = 2.5
FEATURE [PartDesign::Pocket] Pocket058
  BaseFeature = -> Pad111
  Direction = (0,0,-1)
  Length = 1.5
  Length2 = 5
  Profile = -> Sketch147
  ReferenceAxis = -> Sketch147 [N_Axis]
  Refine = true
  Suppressed = false
  Type = 0
FEATURE [Sketcher::SketchObject] Sketch148
  ArcFitTolerance = 1e-06
  AttachmentSupport = -> [Pocket058]
  ExternalGeometry = -> [Pocket058]
  FullyConstrained = true
  MakeInternals = false
  MapMode = 5
  Placement = pos=(0,0,-6.5) rot=(0,0,1;0rad)
  sketch-geometry (1):
    g0: Circle CenterX=18 CenterY=20.4 CenterZ=0 NormalX=0 NormalY=0 NormalZ=1 AngleXU=0 Radius=1
  constraints (2):
    c: Coincident(g0,g-3)
    c: Diameter(g0) = 2
FEATURE [PartDesign::Pocket] Pocket059
  BaseFeature = -> Pocket058
  Direction = (0,0,-1)
  Length = 5
  Length2 = 5
  Profile = -> Sketch148
  ReferenceAxis = -> Sketch148 [N_Axis]
  Refine = true
  Suppressed = false
  Type = 0
FEATURE [Sketcher::SketchObject] Sketch149
  ArcFitTolerance = 1e-06
  AttachmentSupport = -> [Pocket059]
  ExternalGeometry = -> [Pocket059]
  FullyConstrained = true
  MakeInternals = false
  MapMode = 5
  Placement = pos=(0,0,-8) rot=(0,0,1;0rad)
  sketch-geometry (8):
    g0: LineSegment StartX=27 StartY=20.2 StartZ=0 EndX=27 EndY=19.2 EndZ=0
    g1: LineSegment StartX=27 StartY=19.2 StartZ=0 EndX=21.2879 EndY=19.2 EndZ=0
    g2: LineSegment StartX=27 StartY=20.2 StartZ=0 EndX=21.4943 EndY=20.2 EndZ=0
    g3: ArcOfCircle CenterX=18 CenterY=20.4 CenterZ=0 NormalX=0 NormalY=0 NormalZ=1 AngleXU=0 Radius=3.49996 StartAngle=5.93323 EndAngle=6.22601
    g4: LineSegment StartX=9 StartY=19.2 StartZ=0 EndX=9 EndY=20.2 EndZ=0
    g5: LineSegment StartX=9 StartY=19.2 StartZ=0 EndX=14.7121 EndY=19.2 EndZ=0
    g6: LineSegment StartX=9 StartY=20.2 StartZ=0 EndX=14.5057 EndY=20.2 EndZ=0
    g7: ArcOfCircle CenterX=18 CenterY=20.4 CenterZ=0 NormalX=0 NormalY=0 NormalZ=1 AngleXU=0 Radius=3.49997 StartAngle=3.19877 EndAngle=3.49155
  constraints (22):
    c: PointOnObject(g0,g-8)
    c: Coincident(g0,g-8)
    c: Coincident(g1,g0)
    c: Coincident(g1,g-7)
    c: PointOnObject(g2,g-6)
    c: Coincident(g2,g0)
    c: DistanceY(g0,g0) = 1
    c: Horizontal(g2)
    c: Coincident(g3,g1)
    c: Coincident(g3,g2)
    c: Tangent(g3,g-6)
    c: Coincident(g4,g-5)
    c: PointOnObject(g4,g-5)
    c: Coincident(g5,g4)
    c: Coincident(g5,g-4)
    c: DistanceY(g4,g4) = 1
    c: Coincident(g6,g4)
    c: PointOnObject(g6,g-3)
    c: Horizontal(g6)
    c: Coincident(g7,g5)
    c: Coincident(g7,g6)
    c: Tangent(g7,g-3)
FEATURE [PartDesign::Pad] Pad112
  BaseFeature = -> Pocket059
  Direction = (0,0,1)
  Length = 2
  Length2 = 10
  Profile = -> Sketch149
  ReferenceAxis = -> Sketch149 [N_Axis]
  Refine = true
  Suppressed = false
  Type = 0
FEATURE [Sketcher::SketchObject] Sketch150
  ArcFitTolerance = 1e-06
  AttachmentSupport = -> [Pad112]
  ExternalGeometry = -> [Pad112]
  FullyConstrained = true
  MakeInternals = false
  MapMode = 5
  Placement = pos=(0,0,-6) rot=(0,0,1;0rad)
  sketch-geometry (1):
    g0: Circle CenterX=18 CenterY=4.95 CenterZ=0 NormalX=0 NormalY=0 NormalZ=1 AngleXU=0 Radius=2.4
  constraints (4):
    c: DistanceX(g-7,g-5) = 14
    c: DistanceX(g-7,g0) = 7
    c: Diameter(g0) = 4.8
    c: DistanceY(g-6,g0) = 2.95
FEATURE [PartDesign::Pad] Pad113
  BaseFeature = -> Pad112
  Direction = (0,0,1)
  Length = 4
  Length2 = 10
  Profile = -> Sketch150
  ReferenceAxis = -> Sketch150 [N_Axis]
  Refine = true
  Suppressed = false
  Type = 0
FEATURE [Sketcher::SketchObject] Sketch151
  ArcFitTolerance = 1e-06
  AttachmentSupport = -> [Pad113]
  ExternalGeometry = -> [Pad113]
  FullyConstrained = true
  MakeInternals = false
  MapMode = 5
  Placement = pos=(0,0,-2) rot=(0,0,1;0rad)
  sketch-geometry (1):
    g0: Circle CenterX=18 CenterY=4.95 CenterZ=0 NormalX=0 NormalY=0 NormalZ=1 AngleXU=0 Radius=0.75
  constraints (2):
    c: Coincident(g0,g-3)
    c: Radius(g0) = 0.75
FEATURE [PartDesign::Pocket] Pocket060
  BaseFeature = -> Pad113
  Direction = (0,0,-1)
  Length = 5
  Length2 = 5
  Profile = -> Sketch151
  ReferenceAxis = -> Sketch151 [N_Axis]
  Refine = true
  Suppressed = false
  Type = 0
FEATURE [Sketcher::SketchObject] Sketch152
  ArcFitTolerance = 1e-06
  AttachmentSupport = -> [Pocket060]
  ExternalGeometry = -> [Pocket060]
  FullyConstrained = true
  MakeInternals = false
  MapMode = 5
  Placement = pos=(0,0,-8) rot=(1,0,0;3.14159rad)
  sketch-geometry (4):
    g0: LineSegment StartX=7 StartY=-17.2 StartZ=0 EndX=7 EndY=-19.2 EndZ=0
    g1: LineSegment StartX=7 StartY=-19.2 StartZ=0 EndX=29 EndY=-19.2 EndZ=0
    g2: LineSegment StartX=29 StartY=-19.2 StartZ=0 EndX=29 EndY=-17.2 EndZ=0
    g3: LineSegment StartX=29 StartY=-17.2 StartZ=0 EndX=7 EndY=-17.2 EndZ=0
  constraints (10):
    c: Coincident(g0,g1)
    c: Coincident(g1,g2)
    c: Coincident(g2,g3)
    c: Coincident(g3,g0)
    c: Vertical(g0)
    c: Vertical(g2)
    c: Horizontal(g1)
    c: Horizontal(g3)
    c: Coincident(g0,g-4)
    c: Coincident(g1,g-3)
FEATURE [PartDesign::Pad] Pad114
  BaseFeature = -> Pocket060
  Direction = (0,0,-1)
  Length = 2
  Length2 = 10
  Profile = -> Sketch152
  ReferenceAxis = -> Sketch152 [N_Axis]
  Refine = true
  Suppressed = false
  Type = 0
FEATURE [Sketcher::SketchObject] Sketch153
  ArcFitTolerance = 1e-06
  AttachmentSupport = -> [Pad114]
  ExternalGeometry = -> [Pad114]
  FullyConstrained = true
  MakeInternals = false
  MapMode = 5
  Placement = pos=(0,0,-10) rot=(1,0,0;3.14159rad)
  sketch-geometry (1):
    g0: Circle CenterX=18 CenterY=-20.4 CenterZ=0 NormalX=0 NormalY=0 NormalZ=1 AngleXU=0 Radius=2.25
  constraints (2):
    c: Coincident(g0,g-3)
    c: Diameter(g0) = 4.5
FEATURE [PartDesign::Body] Body010  label="Front_Torso"
  AllowCompound = false
  Group = -> [Binder005,Sketch133,Pad101,Sketch134,Pad102,Sketch135,Pad103,Pad104,Sketch136,Pad105,Sketch137,Pad106,Sketch138,Pad107,Sketch139,Pocket053,Sketch140,Pocket054,Sketch141,Pocket055,Sketch142,Pocket056,Pad108,Sketch143,Pocket057,Sketch144,Pad109,Sketch145,Pad110,Sketch146,Pad111,Sketch147,Pocket058,Sketch148,Pocket059,Sketch149,Pad112,Sketch150,Pad113,Sketch151,Pocket060,Sketch152,Pad114,Sketch153,+24 more]
  Origin = -> Origin010
  Tip = -> Fillet006
COMPONENT P11 — recipe-attached ("Left_Arm", modeled in this document).
Construction recipe (the document's own serialized feature program — sketch geometry with constraints, then the solid features built on it; lengths are millimeters unless a unit is written):

FEATURE [PartDesign::SubShapeBinder] Binder006
  BindCopyOnChange = 0
  BindMode = 2
  ClaimChildren = false
  Context = -> Body011 [Binder006.]
  Fuse = false
  MakeFace = true
  OffsetFill = false
  OffsetIntersection = false
  OffsetJoinType = 0
  OffsetOpenResult = false
  PartialLoad = false
  Refine = true
  Relative = true
  _Version = 2
FEATURE [Sketcher::SketchObject] Sketch165
  ArcFitTolerance = 1e-06
  AttachmentSupport = -> [Binder006]
  ExternalGeometry = -> [Binder006]
  FullyConstrained = true
  MakeInternals = false
  MapMode = 5
  Placement = pos=(0,0,0) rot=(1,0,0;3.14159rad)
  sketch-geometry (4):
    g0: LineSegment StartX=7 StartY=-41.35 StartZ=0 EndX=7 EndY=-10.35 EndZ=0
    g1: LineSegment StartX=7 StartY=-10.35 StartZ=0 EndX=5 EndY=-10.35 EndZ=0
    g2: LineSegment StartX=5 StartY=-10.35 StartZ=0 EndX=5 EndY=-41.35 EndZ=0
    g3: LineSegment StartX=7 StartY=-41.35 StartZ=0 EndX=5 EndY=-41.35 EndZ=0
  constraints (12):
    c: PointOnObject(g0,g-3)
    c: PointOnObject(g0,g-5)
    c: Coincident(g1,g0)
    c: Horizontal(g1)
    c: Coincident(g2,g1)
    c: Vertical(g2)
    c: Coincident(g3,g0)
    c: Coincident(g3,g2)
    c: Horizontal(g3)
    c: DistanceY(g-4,g0) = 0.05
    c: DistanceY(g0,g-6) = 0.05
    c: DistanceX(g1,g1) = 2
FEATURE [PartDesign::Pad] Pad116
  Direction = (0,0,-1)
  Length = 10
  Length2 = 10
  Profile = -> Sketch165
  ReferenceAxis = -> Sketch165 [N_Axis]
  Refine = true
  Suppressed = false
  Type = 0
FEATURE [Sketcher::SketchObject] Sketch166
  ArcFitTolerance = 1e-06
  AttachmentSupport = -> [Pad116]
  ExternalGeometry = -> [Pad116]
  FullyConstrained = true
  MakeInternals = false
  MapMode = 5
  Placement = pos=(7,-4e-16,0) rot=(0.57735,0.57735,0.57735;2.0944rad)
  sketch-geometry (4):
    g0: LineSegment StartX=10.35 StartY=-2 StartZ=0 EndX=3.05 EndY=-2 EndZ=0
    g1: LineSegment StartX=3.05 StartY=-2 StartZ=0 EndX=3.05 EndY=-10 EndZ=0
    g2: LineSegment StartX=3.05 StartY=-10 StartZ=0 EndX=10.35 EndY=-10 EndZ=0
    g3: LineSegment StartX=10.35 StartY=-10 StartZ=0 EndX=10.35 EndY=-2 EndZ=0
  constraints (11):
    c: Coincident(g0,g1)
    c: Coincident(g1,g2)
    c: Coincident(g2,g3)
    c: Coincident(g3,g0)
    c: Horizontal(g0)
    c: Horizontal(g2)
    c: Vertical(g1)
    c: Vertical(g3)
    c: DistanceX(g0,g0) = 7.3
    c: Coincident(g2,g-3)
    c: DistanceY(g1,g1) = 8
FEATURE [PartDesign::Pad] Pad117
  BaseFeature = -> Pad116
  Direction = (1,0,0)
  Length = 7
  Length2 = 10
  Profile = -> Sketch166
  ReferenceAxis = -> Sketch166 [N_Axis]
  Refine = true
  Reversed = true
  Suppressed = false
  Type = 0
FEATURE [PartDesign::Pocket] Pocket072
  BaseFeature = -> Pad117
  Direction = (0,-1,0)
  Length = 0.05
  Length2 = 5
  Profile = -> Pad117 [Face7]
  Refine = true
  Suppressed = false
  Type = 0
FEATURE [Sketcher::SketchObject] Sketch167
  ArcFitTolerance = 1e-06
  AttachmentSupport = -> [Pocket072]
  ExternalGeometry = -> [Pocket072]
  FullyConstrained = true
  MakeInternals = false
  MapMode = 5
  Placement = pos=(5,0,0) rot=(0.57735,-0.57735,-0.57735;2.0944rad)
  sketch-geometry (7):
    g0: ArcOfCircle CenterX=-33.95 CenterY=-7 CenterZ=0 NormalX=0 NormalY=0 NormalZ=1 AngleXU=0 Radius=5 StartAngle=3.78509 EndAngle=5.63968
    g1: ArcOfCircle CenterX=-20.75 CenterY=-7 CenterZ=0 NormalX=0 NormalY=0 NormalZ=1 AngleXU=0 Radius=5 StartAngle=3.78509 EndAngle=5.63968
    g2: LineSegment [constr] StartX=-10.3 StartY=-12 StartZ=0 EndX=-41.35 EndY=-12 EndZ=0
    g3: LineSegment [constr] StartX=-10.3 StartY=-12 StartZ=0 EndX=-10.3 EndY=-10 EndZ=0
    g4: LineSegment [constr] StartX=-41.35 StartY=-10 StartZ=0 EndX=-41.35 EndY=-12 EndZ=0
    g5: LineSegment StartX=-24.75 StartY=-10 StartZ=0 EndX=-16.75 EndY=-10 EndZ=0
    g6: LineSegment StartX=-37.95 StartY=-10 StartZ=0 EndX=-29.95 EndY=-10 EndZ=0
  constraints (22):
    c: PointOnObject(g0,g-3)
    c: PointOnObject(g1,g-3)
    c: PointOnObject(g1,g-3)
    c: Radius(g0) = 5
    c: Radius(g1) = 5
    c: Horizontal(g2)
    c: Tangent(g2,g0)
    c: Coincident(g3,g2)
    c: Coincident(g3,g-4)
    c: Vertical(g3)
    c: DistanceY(g3,g3) = 2
    c: Tangent(g1,g2)
    c: Coincident(g4,g-3)
    c: Coincident(g4,g2)
    c: Vertical(g4)
    c: PointOnObject(g0,g-3)
    c: DistanceX(g4,g0) = 3.4
    c: DistanceX(g0,g1) = 5.2
    c: Coincident(g5,g1)
    c: Coincident(g5,g1)
    c: Coincident(g6,g0)
    c: Coincident(g6,g0)
FEATURE [PartDesign::Pad] Pad118
  BaseFeature = -> Pocket072
  Direction = (-1,0,0)
  Length = 2
  Length2 = 10
  Profile = -> Sketch167
  ReferenceAxis = -> Sketch167 [N_Axis]
  Refine = true
  Reversed = true
  Suppressed = false
  Type = 0
FEATURE [Sketcher::SketchObject] Sketch168
  ArcFitTolerance = 1e-06
  AttachmentSupport = -> [Pad118]
  ExternalGeometry = -> [Pad118]
  FullyConstrained = true
  MakeInternals = false
  MapMode = 5
  Placement = pos=(5,0,0) rot=(0.57735,-0.57735,-0.57735;2.0944rad)
  sketch-geometry (6):
    g0: LineSegment StartX=-10.3 StartY=-10 StartZ=0 EndX=-12.05 EndY=-10 EndZ=0
    g1: LineSegment StartX=-12.05 StartY=-10 StartZ=0 EndX=-12.05 EndY=0 EndZ=0
    g2: LineSegment StartX=-12.05 StartY=0 StartZ=0 EndX=-10.35 EndY=0 EndZ=0
    g3: LineSegment StartX=-10.35 StartY=0 StartZ=0 EndX=-10.35 EndY=-2 EndZ=0
    g4: LineSegment StartX=-10.35 StartY=-2 StartZ=0 EndX=-10.3 EndY=-2 EndZ=0
    g5: LineSegment StartX=-10.3 StartY=-2 StartZ=0 EndX=-10.3 EndY=-10 EndZ=0
  constraints (14):
    c: Coincident(g0,g-5)
    c: PointOnObject(g0,g-5)
    c: DistanceX(g0,g0) = 1.75
    c: Coincident(g1,g0)
    c: PointOnObject(g1,g-6)
    c: Vertical(g1)
    c: Coincident(g2,g1)
    c: Coincident(g2,g-6)
    c: Coincident(g3,g2)
    c: Coincident(g3,g-4)
    c: Coincident(g4,g3)
    c: Coincident(g4,g-3)
    c: Coincident(g5,g4)
    c: Coincident(g5,g0)
FEATURE [PartDesign::Pad] Pad119
  BaseFeature = -> Pad118
  Direction = (-1,0,0)
  Length = 5
  Length2 = 10
  Profile = -> Sketch168
  ReferenceAxis = -> Sketch168 [N_Axis]
  Refine = true
  Suppressed = false
  Type = 0
FEATURE [Sketcher::SketchObject] Sketch169
  ArcFitTolerance = 1e-06
  AttachmentSupport = -> [Pad119]
  ExternalGeometry = -> [Pad119]
  FullyConstrained = true
  MakeInternals = false
  MapMode = 5
  Placement = pos=(5,0,0) rot=(0.57735,-0.57735,-0.57735;2.0944rad)
  sketch-geometry (3):
    g0: LineSegment StartX=-12.05 StartY=0 StartZ=0 EndX=-16.35 EndY=0 EndZ=0
    g1: LineSegment StartX=-16.35 StartY=0 StartZ=0 EndX=-12.05 EndY=-4.3 EndZ=0
    g2: LineSegment StartX=-12.05 StartY=-4.3 StartZ=0 EndX=-12.05 EndY=0 EndZ=0
  constraints (9):
    c: PointOnObject(g0,g-3)
    c: PointOnObject(g0,g-3)
    c: Coincident(g1,g0)
    c: PointOnObject(g1,g-4)
    c: Coincident(g2,g1)
    c: Coincident(g2,g0)
    c: Vertical(g2)
    c: DistanceX(g0,g0) = 4.3
    c: Angle(g1,g0) = 0.785398
FEATURE [PartDesign::Pad] Pad120
  BaseFeature = -> Pad119
  Direction = (-1,0,0)
  Length = 5
  Length2 = 10
  Profile = -> Sketch169
  ReferenceAxis = -> Sketch169 [N_Axis]
  Refine = true
  Suppressed = false
  Type = 0
FEATURE [Sketcher::SketchObject] Sketch170
  ArcFitTolerance = 1e-06
  AttachmentSupport = -> [Pad120]
  ExternalGeometry = -> [Pad120]
  FullyConstrained = true
  MakeInternals = false
  MapMode = 5
  Placement = pos=(5,0,0) rot=(0.57735,-0.57735,-0.57735;2.0944rad)
  sketch-geometry (3):
    g0: LineSegment StartX=-41.35 StartY=0 StartZ=0 EndX=-37.35 EndY=0 EndZ=0
    g1: LineSegment StartX=-37.35 StartY=0 StartZ=0 EndX=-41.35 EndY=-4 EndZ=0
    g2: LineSegment StartX=-41.35 StartY=-4 StartZ=0 EndX=-41.35 EndY=0 EndZ=0
  constraints (8):
    c: Coincident(g0,g-4)
    c: PointOnObject(g0,g-3)
    c: Coincident(g1,g0)
    c: Coincident(g2,g1)
    c: Coincident(g2,g0)
    c: Vertical(g2)
    c: DistanceY(g2,g2) = 4
    c: DistanceX(g0,g0) = 4
FEATURE [PartDesign::Pad] Pad121
  BaseFeature = -> Pad120
  Direction = (-1,0,0)
  Length = 5
  Length2 = 10
  Profile = -> Sketch170
  ReferenceAxis = -> Sketch170 [N_Axis]
  Refine = true
  Suppressed = false
  Type = 0
FEATURE [Sketcher::SketchObject] Sketch171
  ArcFitTolerance = 1e-06
  AttachmentSupport = -> [Pad121]
  ExternalGeometry = -> [Pad121]
  FullyConstrained = true
  MakeInternals = false
  MapMode = 5
  Placement = pos=(7,0,0) rot=(0.57735,0.57735,0.57735;2.0944rad)
  sketch-geometry (1):
    g0: Circle CenterX=30.35 CenterY=-4 CenterZ=0 NormalX=0 NormalY=0 NormalZ=1 AngleXU=0 Radius=4
  constraints (3):
    c: Diameter(g0) = 8
    c: Tangent(g0,g-3)
    c: DistanceX(g0,g-3) = 11
FEATURE [PartDesign::Pad] Pad122
  BaseFeature = -> Pad121
  Direction = (1,0,0)
  Length = 5
  Length2 = 10
  Profile = -> Sketch171
  ReferenceAxis = -> Sketch171 [N_Axis]
  Refine = true
  Suppressed = false
  Type = 0
FEATURE [Sketcher::SketchObject] Sketch172
  ArcFitTolerance = 1e-06
  AttachmentSupport = -> [Pad122]
  ExternalGeometry = -> [Pad122]
  FullyConstrained = true
  MakeInternals = false
  MapMode = 5
  Placement = pos=(5,0,0) rot=(0.57735,-0.57735,-0.57735;2.0944rad)
  sketch-geometry (1):
    g0: Circle CenterX=-30.35 CenterY=-4 CenterZ=0 NormalX=0 NormalY=0 NormalZ=1 AngleXU=0 Radius=2.1
  constraints (2):
    c: Coincident(g0,g-3)
    c: Diameter(g0) = 4.2
FEATURE [PartDesign::Pocket] Pocket073
  BaseFeature = -> Pad122
  Direction = (1,0,0)
  Length = 5
  Length2 = 5
  Profile = -> Sketch172
  ReferenceAxis = -> Sketch172 [N_Axis]
  Refine = true
  Suppressed = false
  Type = 0
FEATURE [Sketcher::SketchObject] Sketch173
  ArcFitTolerance = 1e-06
  AttachmentSupport = -> [Pocket073]
  ExternalGeometry = -> [Pocket073]
  FullyConstrained = true
  MakeInternals = false
  MapMode = 5
  Placement = pos=(12,0,0) rot=(0.57735,0.57735,0.57735;2.0944rad)
  sketch-geometry (1):
    g0: Circle CenterX=30.35 CenterY=-4 CenterZ=0 NormalX=0 NormalY=0 NormalZ=1 AngleXU=0 Radius=1.4
  constraints (2):
    c: Coincident(g0,g-3)
    c: Diameter(g0) = 2.8
FEATURE [PartDesign::Pocket] Pocket074
  BaseFeature = -> Pocket073
  Direction = (-1,0,0)
  Length = 5
  Length2 = 5
  Profile = -> Sketch173
  ReferenceAxis = -> Sketch173 [N_Axis]
  Refine = true
  Suppressed = false
  Type = 0
FEATURE [Sketcher::SketchObject] Sketch174
  ArcFitTolerance = 1e-06
  AttachmentSupport = -> [Pocket074]
  ExternalGeometry = -> [Pocket074]
  FullyConstrained = true
  MakeInternals = false
  MapMode = 5
  Placement = pos=(5,0,0) rot=(0.57735,-0.57735,-0.57735;2.0944rad)
  sketch-geometry (2):
    g0: Circle CenterX=-33.95 CenterY=-7 CenterZ=0 NormalX=0 NormalY=0 NormalZ=1 AngleXU=0 Radius=0.75
    g1: Circle CenterX=-20.75 CenterY=-7 CenterZ=0 NormalX=0 NormalY=0 NormalZ=1 AngleXU=0 Radius=0.75
  constraints (4):
    c: Coincident(g0,g-4)
    c: Coincident(g1,g-3)
    c: Radius(g0) = 0.75
    c: Radius(g1) = 0.75
FEATURE [PartDesign::Pocket] Pocket075
  BaseFeature = -> Pocket074
  Direction = (1,0,0)
  Length = 8
  Length2 = 5
  Profile = -> Sketch174
  ReferenceAxis = -> Sketch174 [N_Axis]
  Refine = true
  Suppressed = false
  Type = 0
FEATURE [Sketcher::SketchObject] Sketch175
  ArcFitTolerance = 1e-06
  AttachmentSupport = -> [Pocket075]
  ExternalGeometry = -> [Pocket075]
  FullyConstrained = true
  MakeInternals = false
  MapMode = 5
  Placement = pos=(0,0,-10) rot=(1,0,0;3.14159rad)
  sketch-geometry (1):
    g0: Circle CenterX=3.55 CenterY=-7.2 CenterZ=0 NormalX=0 NormalY=0 NormalZ=1 AngleXU=0 Radius=1.45
  constraints (3):
    c: Radius(g0) = 1.45
    c: DistanceX(g0,g-4) = 3.45
    c: DistanceY(g0,g-4) = 4.15
FEATURE [PartDesign::Pocket] Pocket076
  BaseFeature = -> Pocket075
  Direction = (0,0,1)
  Length = 6
  Length2 = 5
  Profile = -> Sketch175
  ReferenceAxis = -> Sketch175 [N_Axis]
  Refine = true
  Suppressed = false
  Type = 0
FEATURE [Sketcher::SketchObject] Sketch176
  ArcFitTolerance = 1e-06
  AttachmentSupport = -> [Pocket076]
  ExternalGeometry = -> [Pocket076]
  FullyConstrained = true
  MakeInternals = false
  MapMode = 5
  Placement = pos=(0,0,-10) rot=(1,0,0;3.14159rad)
  sketch-geometry (3):
    g0: LineSegment StartX=9e-16 StartY=-3.05 StartZ=0 EndX=1.5 EndY=-3.05 EndZ=0
    g1: LineSegment StartX=1.5 StartY=-3.05 StartZ=0 EndX=9e-16 EndY=-4.55 EndZ=0
    g2: LineSegment StartX=9e-16 StartY=-4.55 StartZ=0 EndX=9e-16 EndY=-3.05 EndZ=0
  constraints (8):
    c: Coincident(g0,g-4)
    c: PointOnObject(g0,g-3)
    c: Coincident(g1,g0)
    c: PointOnObject(g1,g-4)
    c: Coincident(g2,g1)
    c: Coincident(g2,g0)
    c: DistanceX(g0,g0) = 1.5
    c: DistanceY(g2,g2) = 1.5
FEATURE [PartDesign::Pocket] Pocket077
  BaseFeature = -> Pocket076
  Direction = (0,0,1)
  Length = 8
  Length2 = 5
  Profile = -> Sketch176
  ReferenceAxis = -> Sketch176 [N_Axis]
  Refine = true
  Suppressed = false
  Type = 0
FEATURE [Sketcher::SketchObject] Sketch177
  ArcFitTolerance = 1e-06
  AttachmentSupport = -> [Pocket077]
  ExternalGeometry = -> [Pocket077]
  FullyConstrained = true
  MakeInternals = false
  MapMode = 5
  Placement = pos=(7e-16,0,0) rot=(0.57735,-0.57735,-0.57735;2.0944rad)
  sketch-geometry (4):
    g0: LineSegment StartX=-7.15 StartY=-4.4 StartZ=0 EndX=-10.15 EndY=-4.4 EndZ=0
    g1: LineSegment StartX=-10.15 StartY=-4.4 StartZ=0 EndX=-10.15 EndY=-7.6 EndZ=0
    g2: LineSegment StartX=-10.15 StartY=-7.6 StartZ=0 EndX=-7.15 EndY=-7.6 EndZ=0
    g3: LineSegment StartX=-7.15 StartY=-7.6 StartZ=0 EndX=-7.15 EndY=-4.4 EndZ=0
  constraints (12):
    c: Coincident(g0,g1)
    c: Coincident(g1,g2)
    c: Coincident(g2,g3)
    c: Coincident(g3,g0)
    c: Horizontal(g0)
    c: Horizontal(g2)
    c: Vertical(g1)
    c: Vertical(g3)
    c: DistanceX(g0,g0) = 3
    c: DistanceY(g1,g1) = 3.2
    c: DistanceY(g-3,g2) = 2.4
    c: DistanceX(g-4,g1) = 1.9
FEATURE [PartDesign::Pocket] Pocket078
  BaseFeature = -> Pocket077
  Direction = (1,0,0)
  Length = 1.5
  Length2 = 5
  Profile = -> Sketch177
  ReferenceAxis = -> Sketch177 [N_Axis]
  Refine = true
  Suppressed = false
  Type = 0
FEATURE [Sketcher::SketchObject] Sketch178
  ArcFitTolerance = 1e-06
  AttachmentSupport = -> [Pocket078]
  ExternalGeometry = -> [Pocket078]
  FullyConstrained = true
  MakeInternals = false
  MapMode = 5
  Placement = pos=(2.275,2.275,0) rot=(0.862856,-0.357407,-0.357407;1.71777rad)
  sketch-geometry (12):
    g0: LineSegment StartX=-3.21734 StartY=-3.9 StartZ=0 EndX=-3.21734 EndY=-4.1 EndZ=0
    g1: LineSegment StartX=-3.21734 StartY=-4.1 StartZ=0 EndX=-1.09602 EndY=-4.1 EndZ=0
    g2: LineSegment StartX=-1.09602 StartY=-4.1 StartZ=0 EndX=-1.09602 EndY=-3.9 EndZ=0
    g3: LineSegment StartX=-1.09602 StartY=-3.9 StartZ=0 EndX=-3.21734 EndY=-3.9 EndZ=0
    g4: LineSegment StartX=-3.21734 StartY=-5.9 StartZ=0 EndX=-3.21734 EndY=-6.1 EndZ=0
    g5: LineSegment StartX=-3.21734 StartY=-6.1 StartZ=0 EndX=-1.09602 EndY=-6.1 EndZ=0
    g6: LineSegment StartX=-1.09602 StartY=-6.1 StartZ=0 EndX=-1.09602 EndY=-5.9 EndZ=0
    g7: LineSegment StartX=-1.09602 StartY=-5.9 StartZ=0 EndX=-3.21734 EndY=-5.9 EndZ=0
    g8: LineSegment StartX=-3.21734 StartY=-7.9 StartZ=0 EndX=-3.21734 EndY=-8.1 EndZ=0
    g9: LineSegment StartX=-3.21734 StartY=-8.1 StartZ=0 EndX=-1.09602 EndY=-8.1 EndZ=0
    g10: LineSegment StartX=-1.09602 StartY=-8.1 StartZ=0 EndX=-1.09602 EndY=-7.9 EndZ=0
    g11: LineSegment StartX=-1.09602 StartY=-7.9 StartZ=0 EndX=-3.21734 EndY=-7.9 EndZ=0
  constraints (36):
    c: Coincident(g0,g1)
    c: Coincident(g1,g2)
    c: Coincident(g2,g3)
    c: Coincident(g3,g0)
    c: Vertical(g0)
    c: Vertical(g2)
    c: Horizontal(g1)
    c: Horizontal(g3)
    c: PointOnObject(g0,g-5)
    c: PointOnObject(g1,g-3)
    c: Coincident(g4,g5)
    c: Coincident(g5,g6)
    c: Coincident(g6,g7)
    c: Coincident(g7,g4)
    c: Vertical(g4)
    c: Vertical(g6)
    c: Horizontal(g5)
    c: Horizontal(g7)
    c: PointOnObject(g4,g-5)
    c: Coincident(g8,g9)
    c: Coincident(g9,g10)
    c: Coincident(g10,g11)
    c: Coincident(g11,g8)
    c: Vertical(g8)
    c: Vertical(g10)
    c: Horizontal(g9)
    c: Horizontal(g11)
    c: PointOnObject(g8,g-5)
    c: PointOnObject(g9,g-3)
    c: DistanceY(g6,g6) = 0.2
    c: DistanceY(g10,g10) = 0.2
    c: DistanceY(g2,g2) = 0.2
    c: DistanceY(g6,g-4) = 3.9
    c: PointOnObject(g6,g-3)
    c: DistanceY(g6,g1) = 1.8
    c: DistanceY(g10,g5) = 1.8
FEATURE [PartDesign::Pocket] Pocket079
  BaseFeature = -> Pocket078
  Direction = (0.707107,0.707107,0)
  Length = 0.5
  Length2 = 5
  Profile = -> Sketch178
  ReferenceAxis = -> Sketch178 [N_Axis]
  Refine = true
  Suppressed = false
  Type = 0
FEATURE [Sketcher::SketchObject] Sketch179
  ArcFitTolerance = 1e-06
  AttachmentSupport = -> [Pocket079]
  ExternalGeometry = -> [Pocket079]
  FullyConstrained = true
  MakeInternals = false
  MapMode = 5
  Placement = pos=(0,3.05,0) rot=(1,0,0;1.5708rad)
  sketch-geometry (12):
    g0: LineSegment StartX=1.5 StartY=-3.9 StartZ=0 EndX=1.5 EndY=-4.1 EndZ=0
    g1: LineSegment StartX=1.5 StartY=-4.1 StartZ=0 EndX=7 EndY=-4.1 EndZ=0
    g2: LineSegment StartX=7 StartY=-4.1 StartZ=0 EndX=7 EndY=-3.9 EndZ=0
    g3: LineSegment StartX=7 StartY=-3.9 StartZ=0 EndX=1.5 EndY=-3.9 EndZ=0
    g4: LineSegment StartX=1.5 StartY=-5.9 StartZ=0 EndX=1.5 EndY=-6.1 EndZ=0
    g5: LineSegment StartX=1.5 StartY=-6.1 StartZ=0 EndX=7 EndY=-6.1 EndZ=0
    g6: LineSegment StartX=7 StartY=-6.1 StartZ=0 EndX=7 EndY=-5.9 EndZ=0
    g7: LineSegment StartX=7 StartY=-5.9 StartZ=0 EndX=1.5 EndY=-5.9 EndZ=0
    g8: LineSegment StartX=1.5 StartY=-7.9 StartZ=0 EndX=1.5 EndY=-8.1 EndZ=0
    g9: LineSegment StartX=1.5 StartY=-8.1 StartZ=0 EndX=7 EndY=-8.1 EndZ=0
    g10: LineSegment StartX=7 StartY=-8.1 StartZ=0 EndX=7 EndY=-7.9 EndZ=0
    g11: LineSegment StartX=7 StartY=-7.9 StartZ=0 EndX=1.5 EndY=-7.9 EndZ=0
  constraints (30):
    c: Coincident(g0,g1)
    c: Coincident(g1,g2)
    c: Coincident(g2,g3)
    c: Coincident(g3,g0)
    c: Vertical(g2)
    c: Horizontal(g1)
    c: Horizontal(g3)
    c: Coincident(g0,g-5)
    c: PointOnObject(g1,g-3)
    c: Coincident(g4,g5)
    c: Coincident(g5,g6)
    c: Coincident(g6,g7)
    c: Coincident(g7,g4)
    c: Vertical(g6)
    c: Horizontal(g5)
    c: Horizontal(g7)
    c: Coincident(g4,g-6)
    c: PointOnObject(g5,g-3)
    c: Coincident(g8,g9)
    c: Coincident(g9,g10)
    c: Coincident(g10,g11)
    c: Coincident(g11,g8)
    c: Vertical(g10)
    c: Horizontal(g9)
    c: Horizontal(g11)
    c: Coincident(g8,g-7)
    c: PointOnObject(g9,g-3)
    c: Coincident(g8,g-7)
    c: Coincident(g4,g-6)
    c: Coincident(g0,g-5)
FEATURE [PartDesign::Pocket] Pocket080
  BaseFeature = -> Pocket079
  Direction = (0,1,-2e-16)
  Length = 0.5
  Length2 = 5
  Profile = -> Sketch179
  ReferenceAxis = -> Sketch179 [N_Axis]
  Refine = true
  Suppressed = false
  Type = 0
FEATURE [Sketcher::SketchObject] Sketch180
  ArcFitTolerance = 1e-06
  AttachmentSupport = -> [Pocket080]
  ExternalGeometry = -> [Pocket080]
  FullyConstrained = true
  MakeInternals = false
  MapMode = 5
  Placement = pos=(7,0,0) rot=(0.57735,0.57735,0.57735;2.0944rad)
  sketch-geometry (12):
    g0: LineSegment StartX=3.05 StartY=-3.9 StartZ=0 EndX=3.05 EndY=-4.1 EndZ=0
    g1: LineSegment StartX=3.05 StartY=-4.1 StartZ=0 EndX=7.65 EndY=-4.1 EndZ=0
    g2: LineSegment StartX=7.65 StartY=-4.1 StartZ=0 EndX=7.65 EndY=-3.9 EndZ=0
    g3: LineSegment StartX=7.65 StartY=-3.9 StartZ=0 EndX=3.05 EndY=-3.9 EndZ=0
    g4: LineSegment StartX=3.05 StartY=-5.9 StartZ=0 EndX=3.05 EndY=-6.1 EndZ=0
    g5: LineSegment StartX=3.05 StartY=-6.1 StartZ=0 EndX=7.65 EndY=-6.1 EndZ=0
    g6: LineSegment StartX=7.65 StartY=-6.1 StartZ=0 EndX=7.65 EndY=-5.9 EndZ=0
    g7: LineSegment StartX=7.65 StartY=-5.9 StartZ=0 EndX=3.05 EndY=-5.9 EndZ=0
    g8: LineSegment StartX=7.65 StartY=-6.1 StartZ=0 EndX=7.85 EndY=-6.1 EndZ=0
    g9: LineSegment StartX=7.85 StartY=-6.1 StartZ=0 EndX=7.85 EndY=-2 EndZ=0
    g10: LineSegment StartX=7.85 StartY=-2 StartZ=0 EndX=7.65 EndY=-2 EndZ=0
    g11: LineSegment StartX=7.65 StartY=-2 StartZ=0 EndX=7.65 EndY=-6.1 EndZ=0
  constraints (31):
    c: Coincident(g0,g1)
    c: Coincident(g1,g2)
    c: Coincident(g2,g3)
    c: Coincident(g3,g0)
    c: Vertical(g2)
    c: Horizontal(g1)
    c: Horizontal(g3)
    c: Coincident(g0,g-4)
    c: Coincident(g4,g5)
    c: Coincident(g5,g6)
    c: Coincident(g6,g7)
    c: Coincident(g7,g4)
    c: Vertical(g6)
    c: Horizontal(g5)
    c: Horizontal(g7)
    c: Coincident(g4,g-7)
    c: Coincident(g0,g-7)
    c: Coincident(g4,g-8)
    c: DistanceX(g3,g3) = 4.6
    c: DistanceX(g7,g7) = 4.6
    c: Coincident(g8,g9)
    c: Coincident(g9,g10)
    c: Coincident(g10,g11)
    c: Coincident(g11,g8)
    c: Horizontal(g8)
    c: Horizontal(g10)
    c: Vertical(g9)
    c: Vertical(g11)
    c: Coincident(g8,g5)
    c: PointOnObject(g9,g-3)
    c: DistanceX(g8,g8) = 0.2
FEATURE [PartDesign::Pocket] Pocket081
  BaseFeature = -> Pocket080
  Direction = (-1,0,0)
  Length = 0.5
  Length2 = 5
  Profile = -> Sketch180
  ReferenceAxis = -> Sketch180 [N_Axis]
  Refine = true
  Suppressed = false
  Type = 0
FEATURE [Sketcher::SketchObject] Sketch181
  ArcFitTolerance = 1e-06
  AttachmentSupport = -> [Pocket081]
  ExternalGeometry = -> [Pocket081]
  FullyConstrained = true
  MakeInternals = false
  MapMode = 5
  Placement = pos=(7,0,0) rot=(0.57735,0.57735,0.57735;2.0944rad)
  sketch-geometry (12):
    g0: LineSegment StartX=7.85 StartY=-6.1 StartZ=0 EndX=7.95 EndY=-6.1 EndZ=0
    g1: LineSegment StartX=7.95 StartY=-6.1 StartZ=0 EndX=7.95 EndY=-5.9 EndZ=0
    g2: LineSegment StartX=7.95 StartY=-5.9 StartZ=0 EndX=7.85 EndY=-5.9 EndZ=0
    g3: LineSegment StartX=7.85 StartY=-5.9 StartZ=0 EndX=7.85 EndY=-6.1 EndZ=0
    g4: LineSegment StartX=6.25 StartY=-6.1 StartZ=0 EndX=6.05 EndY=-6.1 EndZ=0
    g5: LineSegment StartX=6.05 StartY=-6.1 StartZ=0 EndX=6.05 EndY=-10 EndZ=0
    g6: LineSegment StartX=6.05 StartY=-10 StartZ=0 EndX=6.25 EndY=-10 EndZ=0
    g7: LineSegment StartX=6.25 StartY=-10 StartZ=0 EndX=6.25 EndY=-6.1 EndZ=0
    g8: LineSegment StartX=3.55 StartY=-8.1 StartZ=0 EndX=6.05 EndY=-8.1 EndZ=0
    g9: LineSegment StartX=6.05 StartY=-8.1 StartZ=0 EndX=6.05 EndY=-7.9 EndZ=0
    g10: LineSegment StartX=6.05 StartY=-7.9 StartZ=0 EndX=3.55 EndY=-7.9 EndZ=0
    g11: LineSegment StartX=3.55 StartY=-7.9 StartZ=0 EndX=3.55 EndY=-8.1 EndZ=0
  constraints (33):
    c: Coincident(g0,g1)
    c: Coincident(g1,g2)
    c: Coincident(g2,g3)
    c: Coincident(g3,g0)
    c: Horizontal(g0)
    c: Horizontal(g2)
    c: Vertical(g1)
    c: Vertical(g3)
    c: Coincident(g0,g-4)
    c: Coincident(g4,g5)
    c: Coincident(g5,g6)
    c: Coincident(g6,g7)
    c: Coincident(g7,g4)
    c: Horizontal(g4)
    c: Horizontal(g6)
    c: Vertical(g5)
    c: Vertical(g7)
    c: PointOnObject(g4,g-3)
    c: PointOnObject(g5,g-5)
    c: DistanceX(g6,g6) = 0.2
    c: DistanceX(g4,g0) = 1.7
    c: Coincident(g8,g9)
    c: Coincident(g9,g10)
    c: Coincident(g10,g11)
    c: Coincident(g11,g8)
    c: Horizontal(g8)
    c: Horizontal(g10)
    c: Vertical(g9)
    c: Coincident(g8,g-6)
    c: PointOnObject(g9,g5)
    c: Coincident(g10,g-6)
    c: DistanceX(g-7,g8) = 3
    c: DistanceY(g1,g1) = 0.2
FEATURE [PartDesign::Pocket] Pocket082
  BaseFeature = -> Pocket081
  Direction = (-1,0,0)
  Length = 0.5
  Length2 = 5
  Profile = -> Sketch181
  ReferenceAxis = -> Sketch181 [N_Axis]
  Refine = true
  Suppressed = false
  Type = 0
FEATURE [Sketcher::SketchObject] Sketch182
  ArcFitTolerance = 1e-06
  AttachmentSupport = -> [Pocket082]
  ExternalGeometry = -> [Pocket082]
  FullyConstrained = true
  MakeInternals = false
  MapMode = 5
  Placement = pos=(7,0,0) rot=(0.57735,0.57735,0.57735;2.0944rad)
  sketch-geometry (12):
    g0: LineSegment StartX=7.95 StartY=-5.9 StartZ=0 EndX=7.95 EndY=-8.1 EndZ=0
    g1: LineSegment StartX=7.95 StartY=-8.1 StartZ=0 EndX=8.15 EndY=-8.1 EndZ=0
    g2: LineSegment StartX=8.15 StartY=-8.1 StartZ=0 EndX=8.15 EndY=-5.9 EndZ=0
    g3: LineSegment StartX=8.15 StartY=-5.9 StartZ=0 EndX=7.95 EndY=-5.9 EndZ=0
    g4: LineSegment StartX=10.35 StartY=-2 StartZ=0 EndX=11.85 EndY=-2 EndZ=0
    g5: LineSegment StartX=11.85 StartY=-2 StartZ=0 EndX=11.85 EndY=-1.8 EndZ=0
    g6: LineSegment StartX=11.85 StartY=-1.8 StartZ=0 EndX=10.35 EndY=-1.8 EndZ=0
    g7: LineSegment StartX=10.35 StartY=-1.8 StartZ=0 EndX=10.35 EndY=-2 EndZ=0
    g8: LineSegment StartX=11.85 StartY=-1.8 StartZ=0 EndX=11.85 EndY=-10 EndZ=0
    g9: LineSegment StartX=11.85 StartY=-10 StartZ=0 EndX=12.05 EndY=-10 EndZ=0
    g10: LineSegment StartX=12.05 StartY=-10 StartZ=0 EndX=12.05 EndY=-1.8 EndZ=0
    g11: LineSegment StartX=12.05 StartY=-1.8 StartZ=0 EndX=11.85 EndY=-1.8 EndZ=0
  constraints (33):
    c: Coincident(g0,g1)
    c: Coincident(g1,g2)
    c: Coincident(g2,g3)
    c: Coincident(g3,g0)
    c: Vertical(g0)
    c: Vertical(g2)
    c: Horizontal(g1)
    c: Horizontal(g3)
    c: Coincident(g0,g-3)
    c: DistanceY(g0,g-4) = 0
    c: DistanceX(g3,g3) = 0.2
    c: Coincident(g4,g5)
    c: Coincident(g5,g6)
    c: Coincident(g6,g7)
    c: Coincident(g7,g4)
    c: Horizontal(g4)
    c: Horizontal(g6)
    c: Vertical(g5)
    c: Vertical(g7)
    c: Coincident(g4,g-5)
    c: Coincident(g8,g9)
    c: Coincident(g9,g10)
    c: Coincident(g10,g11)
    c: Coincident(g11,g8)
    c: Vertical(g8)
    c: Vertical(g10)
    c: Horizontal(g9)
    c: Horizontal(g11)
    c: Coincident(g8,g5)
    c: PointOnObject(g8,g-6)
    c: DistanceX(g9,g9) = 0.2
    c: DistanceY(g7,g7) = 0.2
    c: DistanceX(g-7,g4) = 4
FEATURE [PartDesign::Pocket] Pocket083
  BaseFeature = -> Pocket082
  Direction = (-1,0,0)
  Length = 0.5
  Length2 = 5
  Profile = -> Sketch182
  ReferenceAxis = -> Sketch182 [N_Axis]
  Refine = true
  Suppressed = false
  Type = 0
FEATURE [Sketcher::SketchObject] Sketch183
  ArcFitTolerance = 1e-06
  AttachmentSupport = -> [Pocket083]
  ExternalGeometry = -> [Pocket083]
  FullyConstrained = true
  MakeInternals = false
  MapMode = 5
  Placement = pos=(7,0,0) rot=(0.57735,0.57735,0.57735;2.0944rad)
  sketch-geometry (7):
    g0: LineSegment StartX=11.85 StartY=-6.31716 StartZ=0 EndX=11.85 EndY=-6.11716 EndZ=0
    g1: LineSegment StartX=11.85 StartY=-6.11716 StartZ=0 EndX=9.85 EndY=-6.11716 EndZ=0
    g2: LineSegment StartX=9.93284 StartY=-6.31716 StartZ=0 EndX=11.85 EndY=-6.31716 EndZ=0
    g3: LineSegment StartX=8.15 StartY=-8.1 StartZ=0 EndX=9.93284 EndY=-6.31716 EndZ=0
    g4: LineSegment StartX=9.85 StartY=-6.11716 StartZ=0 EndX=8.15 EndY=-7.81716 EndZ=0
    g5: LineSegment StartX=8.15 StartY=-7.81716 StartZ=0 EndX=8.15 EndY=-8.1 EndZ=0
    g6: LineSegment [constr] StartX=8.85711 StartY=-7.11005 StartZ=0 EndX=8.99853 EndY=-7.25147 EndZ=0
  constraints (21):
    c: Coincident(g0,g1)
    c: Coincident(g2,g0)
    c: Vertical(g0)
    c: Horizontal(g1)
    c: Horizontal(g2)
    c: PointOnObject(g0,g-4)
    c: DistanceY(g2,g1) = 0.2
    c: DistanceX(g1,g1) = 2
    c: Coincident(g3,g-3)
    c: Coincident(g4,g1)
    c: PointOnObject(g4,g-3)
    c: Coincident(g5,g4)
    c: Coincident(g5,g3)
    c: Coincident(g3,g2)
    c: Parallel(g4,g3)
    c: Angle(g4,g-3) = 0.785398
    c: PointOnObject(g6,g4)
    c: PointOnObject(g6,g3)
    c: Angle(g4,g6) = 1.5708
    c: Distance(g6,g4) = 1
    c: Distance(g6) = 0.2
FEATURE [PartDesign::Pocket] Pocket084
  BaseFeature = -> Pocket083
  Direction = (-1,0,0)
  Length = 0.5
  Length2 = 5
  Profile = -> Sketch183
  ReferenceAxis = -> Sketch183 [N_Axis]
  Refine = true
  Suppressed = false
  Type = 0
FEATURE [Sketcher::SketchObject] Sketch184
  ArcFitTolerance = 1e-06
  AttachmentSupport = -> [Pocket084]
  ExternalGeometry = -> [Pocket084]
  FullyConstrained = true
  MakeInternals = false
  MapMode = 5
  Placement = pos=(7e-16,0,0) rot=(0.57735,-0.57735,-0.57735;2.0944rad)
  sketch-geometry (1):
    g0: Circle CenterX=-11.85 CenterY=-2.5 CenterZ=0 NormalX=0 NormalY=0 NormalZ=1 AngleXU=0 Radius=1
  constraints (3):
    c: Diameter(g0) = 2
    c: DistanceX(g0,g-3) = 1.5
    c: DistanceY(g0,g-3) = 0.5
FEATURE [PartDesign::Pocket] Pocket085
  BaseFeature = -> Pocket084
  Direction = (1,0,0)
  Length = 0.5
  Length2 = 5
  Profile = -> Sketch184
  ReferenceAxis = -> Sketch184 [N_Axis]
  Refine = true
  Suppressed = false
  Type = 0
FEATURE [PartDesign::Body] Body011  label="Left_Arm"
  AllowCompound = false
  Group = -> [Binder006,Sketch165,Pad116,Sketch166,Pad117,Pocket072,Sketch167,Pad118,Sketch168,Pad119,Sketch169,Pad120,Sketch170,Pad121,Sketch171,Pad122,Sketch172,Pocket073,Sketch173,Pocket074,Sketch174,Pocket075,Sketch175,Pocket076,Sketch176,Pocket077,Sketch177,Pocket078,Sketch178,Pocket079,Sketch179,Pocket080,Sketch180,Pocket081,Sketch181,Pocket082,Sketch182,Pocket083,Sketch183,Pocket084,Sketch184,Pocket085,+4 more]
  Origin = -> Origin011
  Tip = -> Pocket087
COMPONENT P12 — recipe-attached ("Left_Shoulder", modeled in this document).
Construction recipe (the document's own serialized feature program — sketch geometry with constraints, then the solid features built on it; lengths are millimeters unless a unit is written):

FEATURE [PartDesign::SubShapeBinder] Binder007
  BindCopyOnChange = 0
  BindMode = 2
  ClaimChildren = false
  Context = -> Body012 [Binder007.]
  Fuse = false
  MakeFace = true
  OffsetFill = false
  OffsetIntersection = false
  OffsetJoinType = 0
  OffsetOpenResult = false
  PartialLoad = false
  Refine = true
  Relative = true
  _Version = 2
FEATURE [Sketcher::SketchObject] Sketch185
  ArcFitTolerance = 1e-06
  AttachmentSupport = -> [Binder007]
  ExternalGeometry = -> [Binder007]
  FullyConstrained = true
  MakeInternals = false
  MapMode = 5
  Placement = pos=(12,0,0) rot=(0.57735,0.57735,0.57735;2.0944rad)
  sketch-geometry (4):
    g0: LineSegment StartX=26.35 StartY=-0.05 StartZ=0 EndX=26.35 EndY=-7.25 EndZ=0
    g1: LineSegment StartX=26.35 StartY=-7.25 StartZ=0 EndX=34.35 EndY=-7.25 EndZ=0
    g2: LineSegment StartX=34.35 StartY=-7.25 StartZ=0 EndX=34.35 EndY=-0.05 EndZ=0
    g3: LineSegment StartX=34.35 StartY=-0.05 StartZ=0 EndX=26.35 EndY=-0.05 EndZ=0
  constraints (12):
    c: Coincident(g0,g1)
    c: Coincident(g1,g2)
    c: Coincident(g2,g3)
    c: Coincident(g3,g0)
    c: Vertical(g0)
    c: Vertical(g2)
    c: Horizontal(g1)
    c: Horizontal(g3)
    c: DistanceX(g3,g3) = 8
    c: DistanceY(g0,g0) = 7.2
    c: DistanceX(g0,g-3) = 4
    c: DistanceY(g-3,g0) = 3.95
FEATURE [PartDesign::Pad] Pad123
  Direction = (1,0,0)
  Length = 5.3
  Length2 = 10
  Profile = -> Sketch185
  ReferenceAxis = -> Sketch185 [N_Axis]
  Refine = true
  Suppressed = false
  Type = 0
FEATURE [Sketcher::SketchObject] Sketch186
  ArcFitTolerance = 1e-06
  AttachmentSupport = -> [Pad123]
  ExternalGeometry = -> [Binder007]
  FullyConstrained = true
  MakeInternals = false
  MapMode = 5
  Placement = pos=(12,0,0) rot=(0.57735,-0.57735,-0.57735;2.0944rad)
  sketch-geometry (1):
    g0: Circle CenterX=-30.35 CenterY=-4 CenterZ=0 NormalX=0 NormalY=0 NormalZ=1 AngleXU=0 Radius=0.9
  constraints (2):
    c: Coincident(g0,g-3)
    c: Radius(g0) = 0.9
FEATURE [PartDesign::Pocket] Pocket086
  BaseFeature = -> Pad123
  Direction = (1,0,0)
  Length = 7
  Length2 = 5
  Profile = -> Sketch186
  ReferenceAxis = -> Sketch186 [N_Axis]
  Refine = true
  Suppressed = false
  Type = 0
FEATURE [Sketcher::SketchObject] Sketch187
  ArcFitTolerance = 1e-06
  AttachmentSupport = -> [Pocket086]
  ExternalGeometry = -> [Pocket086]
  FullyConstrained = true
  MakeInternals = false
  MapMode = 5
  Placement = pos=(0,34.35,0) rot=(0,0.707107,0.707107;3.14159rad)
  sketch-geometry (4):
    g0: LineSegment StartX=-17.3 StartY=-0.05 StartZ=0 EndX=-17.3 EndY=-7.25 EndZ=0
    g1: LineSegment StartX=-17.3 StartY=-7.25 StartZ=0 EndX=-16.3 EndY=-7.25 EndZ=0
    g2: LineSegment StartX=-16.3 StartY=-7.25 StartZ=0 EndX=-16.3 EndY=-0.05 EndZ=0
    g3: LineSegment StartX=-16.3 StartY=-0.05 StartZ=0 EndX=-17.3 EndY=-0.05 EndZ=0
  constraints (11):
    c: Coincident(g0,g1)
    c: Coincident(g1,g2)
    c: Coincident(g2,g3)
    c: Coincident(g3,g0)
    c: Vertical(g0)
    c: Vertical(g2)
    c: Horizontal(g1)
    c: Horizontal(g3)
    c: Coincident(g0,g-5)
    c: PointOnObject(g1,g-4)
    c: DistanceX(g1,g1) = 1
FEATURE [PartDesign::Pad] Pad124
  BaseFeature = -> Pocket086
  Direction = (0,1,-2e-16)
  Length = 1.2
  Length2 = 10
  Profile = -> Sketch187
  ReferenceAxis = -> Sketch187 [N_Axis]
  Refine = true
  Suppressed = false
  Type = 0
FEATURE [Sketcher::SketchObject] Sketch188
  ArcFitTolerance = 1e-06
  AttachmentSupport = -> [Pad124]
  ExternalGeometry = -> [Pad124]
  FullyConstrained = true
  MakeInternals = false
  MapMode = 5
  Placement = pos=(0,26.35,0) rot=(1,0,0;1.5708rad)
  sketch-geometry (4):
    g0: LineSegment StartX=17.3 StartY=-0.05 StartZ=0 EndX=16.3 EndY=-0.05 EndZ=0
    g1: LineSegment StartX=16.3 StartY=-0.05 StartZ=0 EndX=16.3 EndY=-7.25 EndZ=0
    g2: LineSegment StartX=16.3 StartY=-7.25 StartZ=0 EndX=17.3 EndY=-7.25 EndZ=0
    g3: LineSegment StartX=17.3 StartY=-7.25 StartZ=0 EndX=17.3 EndY=-0.05 EndZ=0
  constraints (11):
    c: Coincident(g0,g1)
    c: Coincident(g1,g2)
    c: Coincident(g2,g3)
    c: Coincident(g3,g0)
    c: Horizontal(g0)
    c: Horizontal(g2)
    c: Vertical(g1)
    c: Vertical(g3)
    c: Coincident(g0,g-3)
    c: PointOnObject(g1,g-4)
    c: DistanceX(g2,g2) = 1
FEATURE [PartDesign::Pad] Pad125
  BaseFeature = -> Pad124
  Direction = (0,-1,2e-16)
  Length = 1.2
  Length2 = 10
  Profile = -> Sketch188
  ReferenceAxis = -> Sketch188 [N_Axis]
  Refine = true
  Suppressed = false
  Type = 0
FEATURE [PartDesign::Pad] Pad242
  BaseFeature = -> Pad125
  Direction = (3e-16,0,-1)
  Length = 0.1
  Length2 = 10
  Profile = -> Pad125 [Face9]
  Refine = true
  Suppressed = false
  Type = 0
FEATURE [PartDesign::Pad] Pad243
  BaseFeature = -> Pad242
  Direction = (0,0,1)
  Length = 0.05
  Length2 = 10
  Profile = -> Pad242 [Face3]
  Refine = true
  Suppressed = false
  Type = 0
FEATURE [Sketcher::SketchObject] Sketch354
  ArcFitTolerance = 1e-06
  AttachmentSupport = -> [Pad243]
  ExternalGeometry = -> [Pad243]
  FullyConstrained = true
  MakeInternals = false
  MapMode = 5
  Placement = pos=(2.1e-15,0,-7.35) rot=(1,0,0;3.14159rad)
  sketch-geometry (12):
    g0: LineSegment StartX=16.3 StartY=-25.15 StartZ=0 EndX=16.3 EndY=-26.3 EndZ=0
    g1: LineSegment StartX=16.3 StartY=-26.3 StartZ=0 EndX=17.3 EndY=-26.3 EndZ=0
    g2: LineSegment StartX=17.3 StartY=-26.3 StartZ=0 EndX=17.3 EndY=-25.15 EndZ=0
    g3: LineSegment StartX=17.3 StartY=-25.15 StartZ=0 EndX=16.3 EndY=-25.15 EndZ=0
    g4: LineSegment StartX=12 StartY=-28.3 StartZ=0 EndX=12 EndY=-32.4 EndZ=0
    g5: LineSegment StartX=12 StartY=-32.4 StartZ=0 EndX=17.3 EndY=-32.4 EndZ=0
    g6: LineSegment StartX=17.3 StartY=-32.4 StartZ=0 EndX=17.3 EndY=-28.3 EndZ=0
    g7: LineSegment StartX=17.3 StartY=-28.3 StartZ=0 EndX=12 EndY=-28.3 EndZ=0
    g8: LineSegment StartX=16.3 StartY=-34.4 StartZ=0 EndX=16.3 EndY=-35.55 EndZ=0
    g9: LineSegment StartX=16.3 StartY=-35.55 StartZ=0 EndX=17.3 EndY=-35.55 EndZ=0
    g10: LineSegment StartX=17.3 StartY=-35.55 StartZ=0 EndX=17.3 EndY=-34.4 EndZ=0
    g11: LineSegment StartX=17.3 StartY=-34.4 StartZ=0 EndX=16.3 EndY=-34.4 EndZ=0
  constraints (34):
    c: Coincident(g0,g1)
    c: Coincident(g1,g2)
    c: Coincident(g2,g3)
    c: Coincident(g3,g0)
    c: Vertical(g0)
    c: Vertical(g2)
    c: Horizontal(g1)
    c: Horizontal(g3)
    c: Coincident(g0,g-8)
    c: PointOnObject(g1,g-4)
    c: Coincident(g4,g5)
    c: Coincident(g5,g6)
    c: Coincident(g6,g7)
    c: Coincident(g7,g4)
    c: Vertical(g4)
    c: Vertical(g6)
    c: Horizontal(g5)
    c: Horizontal(g7)
    c: PointOnObject(g4,g-5)
    c: PointOnObject(g5,g-4)
    c: Coincident(g8,g9)
    c: Coincident(g9,g10)
    c: Coincident(g10,g11)
    c: Coincident(g11,g8)
    c: Vertical(g8)
    c: Vertical(g10)
    c: Horizontal(g9)
    c: Horizontal(g11)
    c: PointOnObject(g8,g-9)
    c: Coincident(g9,g-10)
    c: DistanceY(g8,g8) = 1.15
    c: DistanceY(g10,g5) = 2
    c: DistanceY(g6,g1) = 2
    c: DistanceY(g1,g2) = 1.15
FEATURE [PartDesign::Pad] Pad254
  BaseFeature = -> Pad243
  Direction = (0,0,-1)
  Length = 0.6
  Length2 = 10
  Profile = -> Sketch354
  ReferenceAxis = -> Sketch354 [N_Axis]
  Refine = true
  Suppressed = false
  Type = 0
FEATURE [PartDesign::Body] Body012  label="Left_Shoulder"
  AllowCompound = false
  Group = -> [Binder007,Sketch185,Pad123,Sketch186,Pocket086,Sketch187,Pad124,Sketch188,Pad125,Pad242,Pad243,Sketch354,Pad254]
  Origin = -> Origin012
  Tip = -> Pad254
